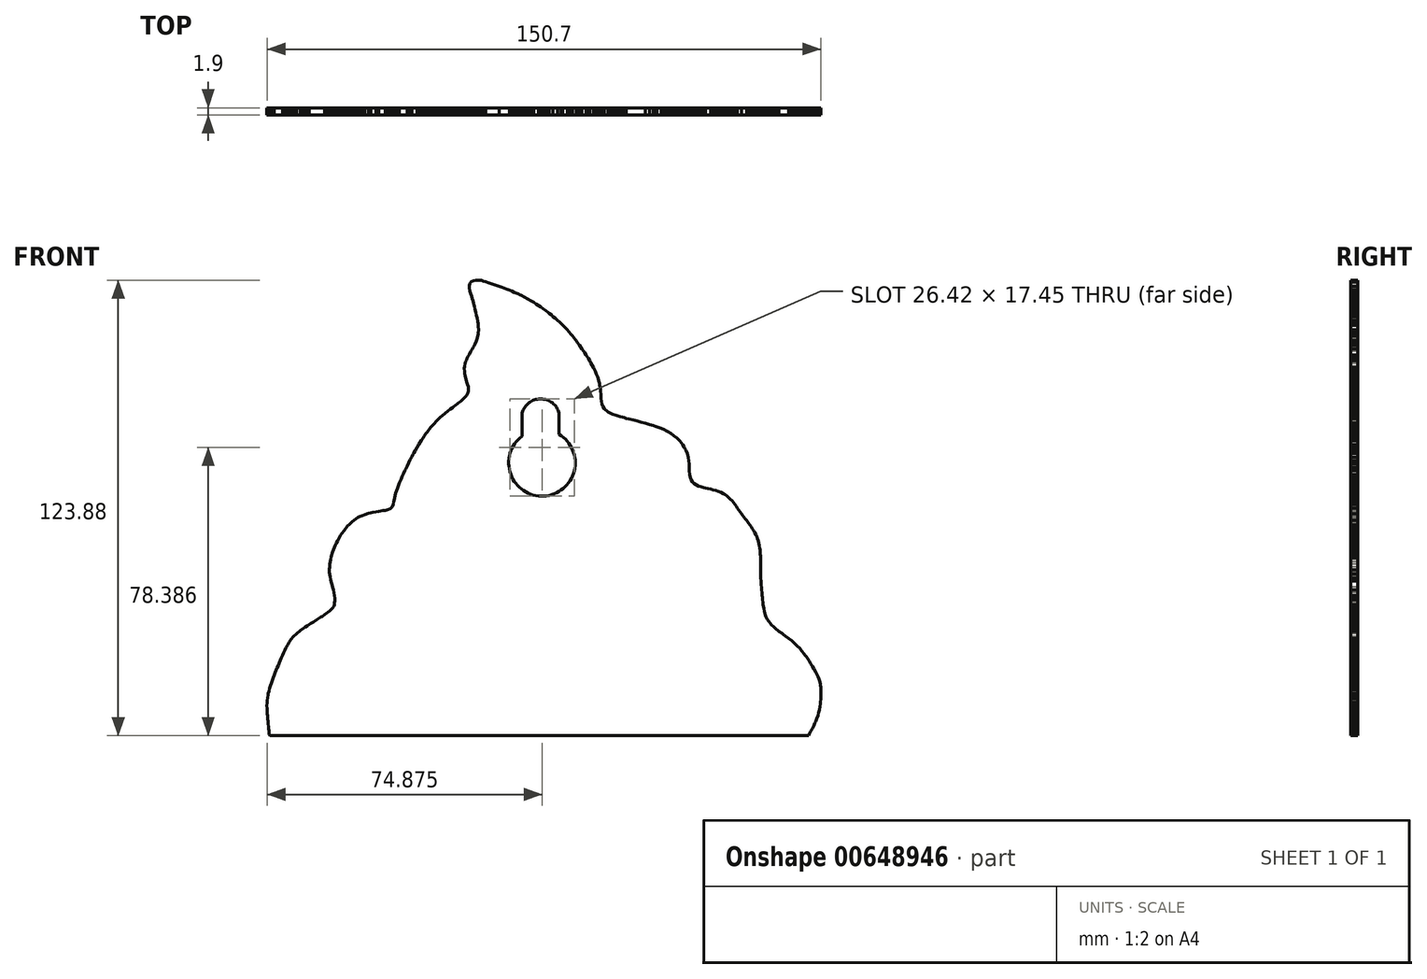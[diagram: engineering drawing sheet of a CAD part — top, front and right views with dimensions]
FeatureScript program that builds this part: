
annotation { "Feature Type Name" : "Feature", "Feature Type Description" : "" }
export const myFeature = defineFeature(function(context is Context, id is Id, definition is map)
    precondition{}
    {
        {
            var Q0;
            Q0=qCreatedBy(makeId("Front.planeOp"),FACE);
            var sketch = newSketch(context, id + "F0", { "sketchPlane" : qUnion([Q0])});
            skLineSegment(sketch, "E0", {"start": v(-3.14, 0.19) * mm, "end": v(-3.1, 0.19) * mm});
            skLineSegment(sketch, "E1", {"start": v(-3.1, 0.19) * mm, "end": v(-3.08, 0.19) * mm});
            skLineSegment(sketch, "E2", {"start": v(-3.08, 0.19) * mm, "end": v(-3.05, 0.19) * mm});
            skLineSegment(sketch, "E3", {"start": v(-3.05, 0.19) * mm, "end": v(-3, 0.19) * mm});
            skLineSegment(sketch, "E4", {"start": v(-3, 0.19) * mm, "end": v(-2.97, 0.19) * mm});
            skLineSegment(sketch, "E5", {"start": v(-2.97, 0.19) * mm, "end": v(-2.94, 0.19) * mm});
            skLineSegment(sketch, "E6", {"start": v(-2.94, 0.19) * mm, "end": v(-2.92, 0.19) * mm});
            skLineSegment(sketch, "E7", {"start": v(-2.92, 0.19) * mm, "end": v(-2.9, 0.19) * mm});
            skLineSegment(sketch, "E8", {"start": v(-2.9, 0.19) * mm, "end": v(-2.86, 0.19) * mm});
            skLineSegment(sketch, "E9", {"start": v(-2.86, 0.19) * mm, "end": v(-2.77, 0.19) * mm});
            skLineSegment(sketch, "E10", {"start": v(-2.77, 0.19) * mm, "end": v(-2.75, 0.19) * mm});
            skLineSegment(sketch, "E11", {"start": v(-2.75, 0.19) * mm, "end": v(-2.72, 0.19) * mm});
            skLineSegment(sketch, "E12", {"start": v(-2.72, 0.19) * mm, "end": v(-2.68, 0.19) * mm});
            skLineSegment(sketch, "E13", {"start": v(-2.68, 0.19) * mm, "end": v(-2.64, 0.19) * mm});
            skLineSegment(sketch, "E14", {"start": v(-2.64, 0.19) * mm, "end": v(-2.53, 0.19) * mm});
            skLineSegment(sketch, "E15", {"start": v(-2.53, 0.19) * mm, "end": v(-2.5, 0.19) * mm});
            skLineSegment(sketch, "E16", {"start": v(-2.5, 0.19) * mm, "end": v(-2.48, 0.19) * mm});
            skLineSegment(sketch, "E17", {"start": v(-2.48, 0.19) * mm, "end": v(-2.46, 0.19) * mm});
            skLineSegment(sketch, "E18", {"start": v(-2.46, 0.19) * mm, "end": v(-2.35, 0.19) * mm});
            skLineSegment(sketch, "E19", {"start": v(-2.35, 0.19) * mm, "end": v(-2.33, 0.19) * mm});
            skLineSegment(sketch, "E20", {"start": v(-2.33, 0.19) * mm, "end": v(-2.3, 0.19) * mm});
            skLineSegment(sketch, "E21", {"start": v(-2.3, 0.19) * mm, "end": v(-2.27, 0.19) * mm});
            skLineSegment(sketch, "E22", {"start": v(-2.27, 0.19) * mm, "end": v(-2.23, 0.19) * mm});
            skLineSegment(sketch, "E23", {"start": v(-2.23, 0.19) * mm, "end": v(-2.2, 0.19) * mm});
            skLineSegment(sketch, "E24", {"start": v(-2.2, 0.19) * mm, "end": v(-2.1, 0.19) * mm});
            skLineSegment(sketch, "E25", {"start": v(-2.1, 0.19) * mm, "end": v(-2.08, 0.19) * mm});
            skLineSegment(sketch, "E26", {"start": v(-2.08, 0.19) * mm, "end": v(-2, 0.19) * mm});
            skLineSegment(sketch, "E27", {"start": v(-2, 0.19) * mm, "end": v(-1.96, 0.19) * mm});
            skLineSegment(sketch, "E28", {"start": v(-1.96, 0.19) * mm, "end": v(-1.94, 0.19) * mm});
            skLineSegment(sketch, "E29", {"start": v(-1.94, 0.19) * mm, "end": v(-1.91, 0.19) * mm});
            skLineSegment(sketch, "E30", {"start": v(-1.91, 0.19) * mm, "end": v(-1.82, 0.19) * mm});
            skLineSegment(sketch, "E31", {"start": v(-1.82, 0.19) * mm, "end": v(-1.8, 0.19) * mm});
            skLineSegment(sketch, "E32", {"start": v(-1.8, 0.19) * mm, "end": v(-1.69, 0.19) * mm});
            skLineSegment(sketch, "E33", {"start": v(-1.69, 0.19) * mm, "end": v(-1.65, 0.19) * mm});
            skLineSegment(sketch, "E34", {"start": v(-1.65, 0.19) * mm, "end": v(-1.62, 0.19) * mm});
            skLineSegment(sketch, "E35", {"start": v(-1.62, 0.19) * mm, "end": v(-1.51, 0.19) * mm});
            skLineSegment(sketch, "E36", {"start": v(-1.51, 0.19) * mm, "end": v(-1.5, 0.19) * mm});
            skLineSegment(sketch, "E37", {"start": v(-1.5, 0.19) * mm, "end": v(-1.45, 0.19) * mm});
            skLineSegment(sketch, "E38", {"start": v(-1.45, 0.19) * mm, "end": v(-1.42, 0.19) * mm});
            skLineSegment(sketch, "E39", {"start": v(-1.42, 0.19) * mm, "end": v(-1.32, 0.19) * mm});
            skLineSegment(sketch, "E40", {"start": v(-1.32, 0.19) * mm, "end": v(-1.3, 0.19) * mm});
            skLineSegment(sketch, "E41", {"start": v(-1.3, 0.19) * mm, "end": v(-1.27, 0.19) * mm});
            skLineSegment(sketch, "E42", {"start": v(-1.27, 0.19) * mm, "end": v(-1.2, 0.19) * mm});
            skLineSegment(sketch, "E43", {"start": v(-1.2, 0.19) * mm, "end": v(-1.18, 0.19) * mm});
            skLineSegment(sketch, "E44", {"start": v(-1.18, 0.19) * mm, "end": v(-1.15, 0.19) * mm});
            skLineSegment(sketch, "E45", {"start": v(-1.15, 0.19) * mm, "end": v(-1.13, 0.19) * mm});
            skLineSegment(sketch, "E46", {"start": v(-1.13, 0.19) * mm, "end": v(-1.1, 0.19) * mm});
            skLineSegment(sketch, "E47", {"start": v(-1.1, 0.19) * mm, "end": v(-1.02, 0.19) * mm});
            skLineSegment(sketch, "E48", {"start": v(-1.02, 0.19) * mm, "end": v(-0.98, 0.19) * mm});
            skLineSegment(sketch, "E49", {"start": v(-0.98, 0.19) * mm, "end": v(-0.95, 0.19) * mm});
            skLineSegment(sketch, "E50", {"start": v(-0.95, 0.19) * mm, "end": v(-0.83, 0.19) * mm});
            skLineSegment(sketch, "E51", {"start": v(-0.83, 0.19) * mm, "end": v(-0.71, 0.19) * mm});
            skLineSegment(sketch, "E52", {"start": v(-0.71, 0.19) * mm, "end": v(-0.69, 0.19) * mm});
            skLineSegment(sketch, "E53", {"start": v(-0.69, 0.19) * mm, "end": v(-0.66, 0.19) * mm});
            skLineSegment(sketch, "E54", {"start": v(-0.66, 0.19) * mm, "end": v(-0.55, 0.19) * mm});
            skLineSegment(sketch, "E55", {"start": v(-0.55, 0.19) * mm, "end": v(-0.44, 0.19) * mm});
            skLineSegment(sketch, "E56", {"start": v(-0.44, 0.19) * mm, "end": v(-0.4, 0.19) * mm});
            skLineSegment(sketch, "E57", {"start": v(-0.4, 0.19) * mm, "end": v(-0.38, 0.19) * mm});
            skLineSegment(sketch, "E58", {"start": v(-0.38, 0.19) * mm, "end": v(-0.29, 0.19) * mm});
            skLineSegment(sketch, "E59", {"start": v(-0.29, 0.19) * mm, "end": v(-0.25, 0.19) * mm});
            skLineSegment(sketch, "E60", {"start": v(-0.25, 0.19) * mm, "end": v(-0.16, 0.19) * mm});
            skLineSegment(sketch, "E61", {"start": v(-0.16, 0.19) * mm, "end": v(-0.14, 0.19) * mm});
            skLineSegment(sketch, "E62", {"start": v(-0.14, 0.19) * mm, "end": v(-0.11, 0.19) * mm});
            skLineSegment(sketch, "E63", {"start": v(-0.11, 0.19) * mm, "end": v(-0.01, 0.19) * mm});
            skLineSegment(sketch, "E64", {"start": v(-0.01, 0.19) * mm, "end": v(0.01, 0.19) * mm});
            skLineSegment(sketch, "E65", {"start": v(0.01, 0.19) * mm, "end": v(0.03, 0.19) * mm});
            skLineSegment(sketch, "E66", {"start": v(0.03, 0.19) * mm, "end": v(0.13, 0.19) * mm});
            skLineSegment(sketch, "E67", {"start": v(0.13, 0.19) * mm, "end": v(0.15, 0.19) * mm});
            skLineSegment(sketch, "E68", {"start": v(0.15, 0.19) * mm, "end": v(0.25, 0.19) * mm});
            skLineSegment(sketch, "E69", {"start": v(0.25, 0.19) * mm, "end": v(0.27, 0.19) * mm});
            skLineSegment(sketch, "E70", {"start": v(0.27, 0.19) * mm, "end": v(0.36, 0.19) * mm});
            skLineSegment(sketch, "E71", {"start": v(0.36, 0.19) * mm, "end": v(0.41, 0.19) * mm});
            skLineSegment(sketch, "E72", {"start": v(0.41, 0.19) * mm, "end": v(0.44, 0.19) * mm});
            skLineSegment(sketch, "E73", {"start": v(0.44, 0.19) * mm, "end": v(0.47, 0.19) * mm});
            skLineSegment(sketch, "E74", {"start": v(0.47, 0.19) * mm, "end": v(0.54, 0.19) * mm});
            skLineSegment(sketch, "E75", {"start": v(0.54, 0.19) * mm, "end": v(0.6, 0.19) * mm});
            skLineSegment(sketch, "E76", {"start": v(0.6, 0.19) * mm, "end": v(0.64, 0.19) * mm});
            skLineSegment(sketch, "E77", {"start": v(0.64, 0.19) * mm, "end": v(0.73, 0.19) * mm});
            skLineSegment(sketch, "E78", {"start": v(0.73, 0.19) * mm, "end": v(0.75, 0.19) * mm});
            skLineSegment(sketch, "E79", {"start": v(0.75, 0.19) * mm, "end": v(0.85, 0.19) * mm});
            skLineSegment(sketch, "E80", {"start": v(0.85, 0.19) * mm, "end": v(0.88, 0.19) * mm});
            skLineSegment(sketch, "E81", {"start": v(0.88, 0.19) * mm, "end": v(0.97, 0.18) * mm});
            skLineSegment(sketch, "E82", {"start": v(0.97, 0.18) * mm, "end": v(1, 0.18) * mm});
            skLineSegment(sketch, "E83", {"start": v(1, 0.18) * mm, "end": v(1.02, 0.18) * mm});
            skLineSegment(sketch, "E84", {"start": v(1.02, 0.18) * mm, "end": v(1.04, 0.18) * mm});
            skLineSegment(sketch, "E85", {"start": v(1.04, 0.18) * mm, "end": v(1.07, 0.18) * mm});
            skLineSegment(sketch, "E86", {"start": v(1.07, 0.18) * mm, "end": v(1.09, 0.18) * mm});
            skLineSegment(sketch, "E87", {"start": v(1.09, 0.18) * mm, "end": v(1.11, 0.18) * mm});
            skLineSegment(sketch, "E88", {"start": v(1.11, 0.18) * mm, "end": v(1.22, 0.18) * mm});
            skLineSegment(sketch, "E89", {"start": v(1.22, 0.18) * mm, "end": v(1.32, 0.18) * mm});
            skLineSegment(sketch, "E90", {"start": v(1.32, 0.18) * mm, "end": v(1.35, 0.18) * mm});
            skLineSegment(sketch, "E91", {"start": v(1.35, 0.18) * mm, "end": v(1.45, 0.18) * mm});
            skLineSegment(sketch, "E92", {"start": v(1.45, 0.18) * mm, "end": v(1.47, 0.18) * mm});
            skLineSegment(sketch, "E93", {"start": v(1.47, 0.18) * mm, "end": v(1.55, 0.18) * mm});
            skLineSegment(sketch, "E94", {"start": v(1.55, 0.18) * mm, "end": v(1.58, 0.18) * mm});
            skLineSegment(sketch, "E95", {"start": v(1.58, 0.18) * mm, "end": v(1.61, 0.18) * mm});
            skLineSegment(sketch, "E96", {"start": v(1.61, 0.18) * mm, "end": v(1.64, 0.18) * mm});
            skLineSegment(sketch, "E97", {"start": v(1.64, 0.18) * mm, "end": v(1.7, 0.18) * mm});
            skLineSegment(sketch, "E98", {"start": v(1.7, 0.18) * mm, "end": v(1.73, 0.18) * mm});
            skLineSegment(sketch, "E99", {"start": v(1.73, 0.18) * mm, "end": v(1.76, 0.18) * mm});
            skLineSegment(sketch, "E100", {"start": v(1.76, 0.18) * mm, "end": v(1.81, 0.18) * mm});
            skLineSegment(sketch, "E101", {"start": v(1.81, 0.18) * mm, "end": v(1.9, 0.18) * mm});
            skLineSegment(sketch, "E102", {"start": v(1.9, 0.18) * mm, "end": v(1.91, 0.18) * mm});
            skLineSegment(sketch, "E103", {"start": v(1.91, 0.18) * mm, "end": v(1.94, 0.18) * mm});
            skLineSegment(sketch, "E104", {"start": v(1.94, 0.18) * mm, "end": v(1.97, 0.18) * mm});
            skLineSegment(sketch, "E105", {"start": v(1.97, 0.18) * mm, "end": v(2.03, 0.18) * mm});
            skLineSegment(sketch, "E106", {"start": v(2.03, 0.18) * mm, "end": v(2.06, 0.18) * mm});
            skLineSegment(sketch, "E107", {"start": v(2.06, 0.18) * mm, "end": v(2.09, 0.18) * mm});
            skLineSegment(sketch, "E108", {"start": v(2.09, 0.18) * mm, "end": v(2.12, 0.18) * mm});
            skLineSegment(sketch, "E109", {"start": v(2.12, 0.18) * mm, "end": v(2.16, 0.18) * mm});
            skLineSegment(sketch, "E110", {"start": v(2.16, 0.18) * mm, "end": v(2.2, 0.18) * mm});
            skLineSegment(sketch, "E111", {"start": v(2.2, 0.18) * mm, "end": v(2.22, 0.18) * mm});
            skLineSegment(sketch, "E112", {"start": v(2.22, 0.18) * mm, "end": v(2.3, 0.18) * mm});
            skLineSegment(sketch, "E113", {"start": v(2.3, 0.18) * mm, "end": v(2.34, 0.18) * mm});
            skLineSegment(sketch, "E114", {"start": v(2.34, 0.18) * mm, "end": v(2.36, 0.18) * mm});
            skLineSegment(sketch, "E115", {"start": v(2.36, 0.18) * mm, "end": v(2.38, 0.18) * mm});
            skLineSegment(sketch, "E116", {"start": v(2.38, 0.18) * mm, "end": v(2.45, 0.18) * mm});
            skLineSegment(sketch, "E117", {"start": v(2.45, 0.18) * mm, "end": v(2.47, 0.18) * mm});
            skLineSegment(sketch, "E118", {"start": v(2.47, 0.18) * mm, "end": v(2.5, 0.18) * mm});
            skLineSegment(sketch, "E119", {"start": v(2.5, 0.18) * mm, "end": v(2.52, 0.18) * mm});
            skLineSegment(sketch, "E120", {"start": v(2.52, 0.18) * mm, "end": v(2.56, 0.18) * mm});
            skLineSegment(sketch, "E121", {"start": v(2.56, 0.18) * mm, "end": v(2.66, 0.18) * mm});
            skLineSegment(sketch, "E122", {"start": v(2.66, 0.18) * mm, "end": v(2.69, 0.18) * mm});
            skLineSegment(sketch, "E123", {"start": v(2.69, 0.18) * mm, "end": v(2.8, 0.18) * mm});
            skLineSegment(sketch, "E124", {"start": v(2.8, 0.18) * mm, "end": v(2.83, 0.18) * mm});
            skLineSegment(sketch, "E125", {"start": v(2.83, 0.18) * mm, "end": v(2.86, 0.18) * mm});
            skLineSegment(sketch, "E126", {"start": v(2.86, 0.18) * mm, "end": v(2.9, 0.18) * mm});
            skLineSegment(sketch, "E127", {"start": v(2.9, 0.18) * mm, "end": v(2.92, 0.18) * mm});
            skLineSegment(sketch, "E128", {"start": v(2.92, 0.18) * mm, "end": v(2.95, 0.18) * mm});
            skLineSegment(sketch, "E129", {"start": v(2.95, 0.18) * mm, "end": v(3.06, 0.18) * mm});
            skLineSegment(sketch, "E130", {"start": v(3.06, 0.18) * mm, "end": v(3.09, 0.18) * mm});
            skLineSegment(sketch, "E131", {"start": v(3.09, 0.18) * mm, "end": v(3.1, 0.18) * mm});
            skLineSegment(sketch, "E132", {"start": v(3.1, 0.18) * mm, "end": v(3.13, 0.18) * mm});
            skLineSegment(sketch, "E133", {"start": v(3.13, 0.18) * mm, "end": v(3.24, 0.18) * mm});
            skLineSegment(sketch, "E134", {"start": v(3.24, 0.18) * mm, "end": v(3.26, 0.18) * mm});
            skLineSegment(sketch, "E135", {"start": v(3.26, 0.18) * mm, "end": v(3.29, 0.18) * mm});
            skLineSegment(sketch, "E136", {"start": v(3.29, 0.18) * mm, "end": v(3.3, 0.18) * mm});
            skLineSegment(sketch, "E137", {"start": v(3.3, 0.18) * mm, "end": v(3.33, 0.18) * mm});
            skLineSegment(sketch, "E138", {"start": v(3.33, 0.18) * mm, "end": v(3.35, 0.18) * mm});
            skLineSegment(sketch, "E139", {"start": v(3.35, 0.18) * mm, "end": v(3.37, 0.18) * mm});
            skLineSegment(sketch, "E140", {"start": v(3.37, 0.18) * mm, "end": v(3.4, 0.18) * mm});
            skLineSegment(sketch, "E141", {"start": v(3.4, 0.18) * mm, "end": v(3.42, 0.18) * mm});
            skLineSegment(sketch, "E142", {"start": v(3.42, 0.18) * mm, "end": v(3.52, 0.18) * mm});
            skLineSegment(sketch, "E143", {"start": v(3.52, 0.18) * mm, "end": v(3.56, 0.18) * mm});
            skLineSegment(sketch, "E144", {"start": v(3.56, 0.18) * mm, "end": v(3.59, 0.18) * mm});
            skLineSegment(sketch, "E145", {"start": v(3.59, 0.18) * mm, "end": v(3.62, 0.18) * mm});
            skLineSegment(sketch, "E146", {"start": v(3.62, 0.18) * mm, "end": v(3.64, 0.18) * mm});
            skLineSegment(sketch, "E147", {"start": v(3.64, 0.18) * mm, "end": v(3.67, 0.18) * mm});
            skLineSegment(sketch, "E148", {"start": v(3.67, 0.18) * mm, "end": v(3.82, 0.18) * mm});
            skLineSegment(sketch, "E149", {"start": v(3.82, 0.18) * mm, "end": v(3.84, 0.18) * mm});
            skLineSegment(sketch, "E150", {"start": v(3.84, 0.18) * mm, "end": v(4, 0.18) * mm});
            skLineSegment(sketch, "E151", {"start": v(4, 0.18) * mm, "end": v(4.03, 0.18) * mm});
            skLineSegment(sketch, "E152", {"start": v(4.03, 0.18) * mm, "end": v(4.06, 0.18) * mm});
            skLineSegment(sketch, "E153", {"start": v(4.06, 0.18) * mm, "end": v(4.08, 0.18) * mm});
            skLineSegment(sketch, "E154", {"start": v(4.08, 0.18) * mm, "end": v(4.1, 0.18) * mm});
            skLineSegment(sketch, "E155", {"start": v(4.1, 0.18) * mm, "end": v(4.14, 0.18) * mm});
            skLineSegment(sketch, "E156", {"start": v(4.14, 0.18) * mm, "end": v(4.26, 0.18) * mm});
            skLineSegment(sketch, "E157", {"start": v(4.26, 0.18) * mm, "end": v(4.37, 0.18) * mm});
            skLineSegment(sketch, "E158", {"start": v(4.37, 0.18) * mm, "end": v(4.41, 0.18) * mm});
            skLineSegment(sketch, "E159", {"start": v(4.41, 0.18) * mm, "end": v(4.47, 0.18) * mm});
            skLineSegment(sketch, "E160", {"start": v(4.47, 0.18) * mm, "end": v(4.49, 0.18) * mm});
            skLineSegment(sketch, "E161", {"start": v(4.49, 0.18) * mm, "end": v(4.5, 0.18) * mm});
            skLineSegment(sketch, "E162", {"start": v(4.5, 0.18) * mm, "end": v(4.55, 0.18) * mm});
            skLineSegment(sketch, "E163", {"start": v(4.55, 0.18) * mm, "end": v(4.57, 0.18) * mm});
            skLineSegment(sketch, "E164", {"start": v(4.57, 0.18) * mm, "end": v(4.58, 0.2) * mm});
            skLineSegment(sketch, "E165", {"start": v(4.58, 0.2) * mm, "end": v(4.6, 0.25) * mm});
            skLineSegment(sketch, "E166", {"start": v(4.6, 0.25) * mm, "end": v(4.61, 0.27) * mm});
            skLineSegment(sketch, "E167", {"start": v(4.61, 0.27) * mm, "end": v(4.62, 0.29) * mm});
            skLineSegment(sketch, "E168", {"start": v(4.62, 0.29) * mm, "end": v(4.64, 0.33) * mm});
            skLineSegment(sketch, "E169", {"start": v(4.64, 0.33) * mm, "end": v(4.66, 0.36) * mm});
            skLineSegment(sketch, "E170", {"start": v(4.66, 0.36) * mm, "end": v(4.67, 0.38) * mm});
            skLineSegment(sketch, "E171", {"start": v(4.67, 0.38) * mm, "end": v(4.68, 0.4) * mm});
            skLineSegment(sketch, "E172", {"start": v(4.68, 0.4) * mm, "end": v(4.69, 0.43) * mm});
            skLineSegment(sketch, "E173", {"start": v(4.69, 0.43) * mm, "end": v(4.7, 0.47) * mm});
            skLineSegment(sketch, "E174", {"start": v(4.7, 0.47) * mm, "end": v(4.72, 0.52) * mm});
            skLineSegment(sketch, "E175", {"start": v(4.72, 0.52) * mm, "end": v(4.73, 0.55) * mm});
            skLineSegment(sketch, "E176", {"start": v(4.73, 0.55) * mm, "end": v(4.73, 0.6) * mm});
            skLineSegment(sketch, "E177", {"start": v(4.73, 0.6) * mm, "end": v(4.74, 0.64) * mm});
            skLineSegment(sketch, "E178", {"start": v(4.74, 0.64) * mm, "end": v(4.74, 0.66) * mm});
            skLineSegment(sketch, "E179", {"start": v(4.74, 0.66) * mm, "end": v(4.75, 0.71) * mm});
            skLineSegment(sketch, "E180", {"start": v(4.75, 0.71) * mm, "end": v(4.75, 0.76) * mm});
            skLineSegment(sketch, "E181", {"start": v(4.75, 0.76) * mm, "end": v(4.75, 0.79) * mm});
            skLineSegment(sketch, "E182", {"start": v(4.75, 0.79) * mm, "end": v(4.75, 0.84) * mm});
            skLineSegment(sketch, "E183", {"start": v(4.75, 0.84) * mm, "end": v(4.74, 0.88) * mm});
            skLineSegment(sketch, "E184", {"start": v(4.74, 0.88) * mm, "end": v(4.74, 0.9) * mm});
            skLineSegment(sketch, "E185", {"start": v(4.74, 0.9) * mm, "end": v(4.74, 0.92) * mm});
            skLineSegment(sketch, "E186", {"start": v(4.74, 0.92) * mm, "end": v(4.73, 0.95) * mm});
            skLineSegment(sketch, "E187", {"start": v(4.73, 0.95) * mm, "end": v(4.72, 1) * mm});
            skLineSegment(sketch, "E188", {"start": v(4.72, 1) * mm, "end": v(4.7, 1.03) * mm});
            skLineSegment(sketch, "E189", {"start": v(4.7, 1.03) * mm, "end": v(4.69, 1.07) * mm});
            skLineSegment(sketch, "E190", {"start": v(4.69, 1.07) * mm, "end": v(4.67, 1.1) * mm});
            skLineSegment(sketch, "E191", {"start": v(4.67, 1.1) * mm, "end": v(4.65, 1.14) * mm});
            skLineSegment(sketch, "E192", {"start": v(4.65, 1.14) * mm, "end": v(4.63, 1.18) * mm});
            skLineSegment(sketch, "E193", {"start": v(4.63, 1.18) * mm, "end": v(4.6, 1.22) * mm});
            skLineSegment(sketch, "E194", {"start": v(4.6, 1.22) * mm, "end": v(4.58, 1.26) * mm});
            skLineSegment(sketch, "E195", {"start": v(4.58, 1.26) * mm, "end": v(4.55, 1.3) * mm});
            skLineSegment(sketch, "E196", {"start": v(4.55, 1.3) * mm, "end": v(4.54, 1.31) * mm});
            skLineSegment(sketch, "E197", {"start": v(4.54, 1.31) * mm, "end": v(4.52, 1.33) * mm});
            skLineSegment(sketch, "E198", {"start": v(4.52, 1.33) * mm, "end": v(4.5, 1.36) * mm});
            skLineSegment(sketch, "E199", {"start": v(4.5, 1.36) * mm, "end": v(4.48, 1.4) * mm});
            skLineSegment(sketch, "E200", {"start": v(4.48, 1.4) * mm, "end": v(4.44, 1.43) * mm});
            skLineSegment(sketch, "E201", {"start": v(4.44, 1.43) * mm, "end": v(4.4, 1.47) * mm});
            skLineSegment(sketch, "E202", {"start": v(4.4, 1.47) * mm, "end": v(4.39, 1.5) * mm});
            skLineSegment(sketch, "E203", {"start": v(4.39, 1.5) * mm, "end": v(4.36, 1.52) * mm});
            skLineSegment(sketch, "E204", {"start": v(4.36, 1.52) * mm, "end": v(4.33, 1.54) * mm});
            skLineSegment(sketch, "E205", {"start": v(4.33, 1.54) * mm, "end": v(4.29, 1.58) * mm});
            skLineSegment(sketch, "E206", {"start": v(4.29, 1.58) * mm, "end": v(4.24, 1.61) * mm});
            skLineSegment(sketch, "E207", {"start": v(4.24, 1.61) * mm, "end": v(4.2, 1.63) * mm});
            skLineSegment(sketch, "E208", {"start": v(4.2, 1.63) * mm, "end": v(4.2, 1.65) * mm});
            skLineSegment(sketch, "E209", {"start": v(4.2, 1.65) * mm, "end": v(4.15, 1.68) * mm});
            skLineSegment(sketch, "E210", {"start": v(4.15, 1.68) * mm, "end": v(4.13, 1.7) * mm});
            skLineSegment(sketch, "E211", {"start": v(4.13, 1.7) * mm, "end": v(4.1, 1.71) * mm});
            skLineSegment(sketch, "E212", {"start": v(4.1, 1.71) * mm, "end": v(4.07, 1.74) * mm});
            skLineSegment(sketch, "E213", {"start": v(4.07, 1.74) * mm, "end": v(4.04, 1.77) * mm});
            skLineSegment(sketch, "E214", {"start": v(4.04, 1.77) * mm, "end": v(4.02, 1.8) * mm});
            skLineSegment(sketch, "E215", {"start": v(4.02, 1.8) * mm, "end": v(4, 1.81) * mm});
            skLineSegment(sketch, "E216", {"start": v(4, 1.81) * mm, "end": v(3.98, 1.85) * mm});
            skLineSegment(sketch, "E217", {"start": v(3.98, 1.85) * mm, "end": v(3.96, 1.9) * mm});
            skLineSegment(sketch, "E218", {"start": v(3.96, 1.9) * mm, "end": v(3.95, 1.91) * mm});
            skLineSegment(sketch, "E219", {"start": v(3.95, 1.91) * mm, "end": v(3.94, 1.94) * mm});
            skLineSegment(sketch, "E220", {"start": v(3.94, 1.94) * mm, "end": v(3.94, 1.96) * mm});
            skLineSegment(sketch, "E221", {"start": v(3.94, 1.96) * mm, "end": v(3.93, 2) * mm});
            skLineSegment(sketch, "E222", {"start": v(3.93, 2) * mm, "end": v(3.92, 2.03) * mm});
            skLineSegment(sketch, "E223", {"start": v(3.92, 2.03) * mm, "end": v(3.92, 2.06) * mm});
            skLineSegment(sketch, "E224", {"start": v(3.92, 2.06) * mm, "end": v(3.92, 2.1) * mm});
            skLineSegment(sketch, "E225", {"start": v(3.92, 2.1) * mm, "end": v(3.91, 2.13) * mm});
            skLineSegment(sketch, "E226", {"start": v(3.91, 2.13) * mm, "end": v(3.9, 2.17) * mm});
            skLineSegment(sketch, "E227", {"start": v(3.9, 2.17) * mm, "end": v(3.9, 2.19) * mm});
            skLineSegment(sketch, "E228", {"start": v(3.9, 2.19) * mm, "end": v(3.9, 2.23) * mm});
            skLineSegment(sketch, "E229", {"start": v(3.9, 2.23) * mm, "end": v(3.9, 2.27) * mm});
            skLineSegment(sketch, "E230", {"start": v(3.9, 2.27) * mm, "end": v(3.9, 2.3) * mm});
            skLineSegment(sketch, "E231", {"start": v(3.9, 2.3) * mm, "end": v(3.9, 2.35) * mm});
            skLineSegment(sketch, "E232", {"start": v(3.9, 2.35) * mm, "end": v(3.9, 2.4) * mm});
            skLineSegment(sketch, "E233", {"start": v(3.9, 2.4) * mm, "end": v(3.89, 2.44) * mm});
            skLineSegment(sketch, "E234", {"start": v(3.89, 2.44) * mm, "end": v(3.89, 2.47) * mm});
            skLineSegment(sketch, "E235", {"start": v(3.89, 2.47) * mm, "end": v(3.89, 2.5) * mm});
            skLineSegment(sketch, "E236", {"start": v(3.89, 2.5) * mm, "end": v(3.89, 2.53) * mm});
            skLineSegment(sketch, "E237", {"start": v(3.89, 2.53) * mm, "end": v(3.88, 2.56) * mm});
            skLineSegment(sketch, "E238", {"start": v(3.88, 2.56) * mm, "end": v(3.88, 2.58) * mm});
            skLineSegment(sketch, "E239", {"start": v(3.88, 2.58) * mm, "end": v(3.88, 2.63) * mm});
            skLineSegment(sketch, "E240", {"start": v(3.88, 2.63) * mm, "end": v(3.88, 2.67) * mm});
            skLineSegment(sketch, "E241", {"start": v(3.88, 2.67) * mm, "end": v(3.88, 2.7) * mm});
            skLineSegment(sketch, "E242", {"start": v(3.88, 2.7) * mm, "end": v(3.88, 2.73) * mm});
            skLineSegment(sketch, "E243", {"start": v(3.88, 2.73) * mm, "end": v(3.88, 2.76) * mm});
            skLineSegment(sketch, "E244", {"start": v(3.88, 2.76) * mm, "end": v(3.88, 2.78) * mm});
            skLineSegment(sketch, "E245", {"start": v(3.88, 2.78) * mm, "end": v(3.88, 2.81) * mm});
            skLineSegment(sketch, "E246", {"start": v(3.88, 2.81) * mm, "end": v(3.88, 2.84) * mm});
            skLineSegment(sketch, "E247", {"start": v(3.88, 2.84) * mm, "end": v(3.87, 2.87) * mm});
            skLineSegment(sketch, "E248", {"start": v(3.87, 2.87) * mm, "end": v(3.87, 2.9) * mm});
            skLineSegment(sketch, "E249", {"start": v(3.87, 2.9) * mm, "end": v(3.86, 2.94) * mm});
            skLineSegment(sketch, "E250", {"start": v(3.86, 2.94) * mm, "end": v(3.85, 2.97) * mm});
            skLineSegment(sketch, "E251", {"start": v(3.85, 2.97) * mm, "end": v(3.84, 3) * mm});
            skLineSegment(sketch, "E252", {"start": v(3.84, 3) * mm, "end": v(3.83, 3.03) * mm});
            skLineSegment(sketch, "E253", {"start": v(3.83, 3.03) * mm, "end": v(3.81, 3.06) * mm});
            skLineSegment(sketch, "E254", {"start": v(3.81, 3.06) * mm, "end": v(3.8, 3.1) * mm});
            skLineSegment(sketch, "E255", {"start": v(3.8, 3.1) * mm, "end": v(3.78, 3.12) * mm});
            skLineSegment(sketch, "E256", {"start": v(3.78, 3.12) * mm, "end": v(3.77, 3.15) * mm});
            skLineSegment(sketch, "E257", {"start": v(3.77, 3.15) * mm, "end": v(3.75, 3.17) * mm});
            skLineSegment(sketch, "E258", {"start": v(3.75, 3.17) * mm, "end": v(3.73, 3.2) * mm});
            skLineSegment(sketch, "E259", {"start": v(3.73, 3.2) * mm, "end": v(3.71, 3.23) * mm});
            skLineSegment(sketch, "E260", {"start": v(3.71, 3.23) * mm, "end": v(3.7, 3.25) * mm});
            skLineSegment(sketch, "E261", {"start": v(3.7, 3.25) * mm, "end": v(3.68, 3.26) * mm});
            skLineSegment(sketch, "E262", {"start": v(3.68, 3.26) * mm, "end": v(3.66, 3.29) * mm});
            skLineSegment(sketch, "E263", {"start": v(3.66, 3.29) * mm, "end": v(3.65, 3.31) * mm});
            skLineSegment(sketch, "E264", {"start": v(3.65, 3.31) * mm, "end": v(3.63, 3.34) * mm});
            skLineSegment(sketch, "E265", {"start": v(3.63, 3.34) * mm, "end": v(3.61, 3.36) * mm});
            skLineSegment(sketch, "E266", {"start": v(3.61, 3.36) * mm, "end": v(3.6, 3.39) * mm});
            skLineSegment(sketch, "E267", {"start": v(3.6, 3.39) * mm, "end": v(3.57, 3.41) * mm});
            skLineSegment(sketch, "E268", {"start": v(3.57, 3.41) * mm, "end": v(3.55, 3.44) * mm});
            skLineSegment(sketch, "E269", {"start": v(3.55, 3.44) * mm, "end": v(3.53, 3.47) * mm});
            skLineSegment(sketch, "E270", {"start": v(3.53, 3.47) * mm, "end": v(3.51, 3.5) * mm});
            skLineSegment(sketch, "E271", {"start": v(3.51, 3.5) * mm, "end": v(3.5, 3.52) * mm});
            skLineSegment(sketch, "E272", {"start": v(3.5, 3.52) * mm, "end": v(3.47, 3.54) * mm});
            skLineSegment(sketch, "E273", {"start": v(3.47, 3.54) * mm, "end": v(3.45, 3.57) * mm});
            skLineSegment(sketch, "E274", {"start": v(3.45, 3.57) * mm, "end": v(3.43, 3.6) * mm});
            skLineSegment(sketch, "E275", {"start": v(3.43, 3.6) * mm, "end": v(3.4, 3.61) * mm});
            skLineSegment(sketch, "E276", {"start": v(3.4, 3.61) * mm, "end": v(3.38, 3.63) * mm});
            skLineSegment(sketch, "E277", {"start": v(3.38, 3.63) * mm, "end": v(3.35, 3.65) * mm});
            skLineSegment(sketch, "E278", {"start": v(3.35, 3.65) * mm, "end": v(3.31, 3.67) * mm});
            skLineSegment(sketch, "E279", {"start": v(3.31, 3.67) * mm, "end": v(3.28, 3.68) * mm});
            skLineSegment(sketch, "E280", {"start": v(3.28, 3.68) * mm, "end": v(3.24, 3.7) * mm});
            skLineSegment(sketch, "E281", {"start": v(3.24, 3.7) * mm, "end": v(3.2, 3.7) * mm});
            skLineSegment(sketch, "E282", {"start": v(3.2, 3.7) * mm, "end": v(3.17, 3.71) * mm});
            skLineSegment(sketch, "E283", {"start": v(3.17, 3.71) * mm, "end": v(3.13, 3.72) * mm});
            skLineSegment(sketch, "E284", {"start": v(3.13, 3.72) * mm, "end": v(3.1, 3.73) * mm});
            skLineSegment(sketch, "E285", {"start": v(3.1, 3.73) * mm, "end": v(3.07, 3.74) * mm});
            skLineSegment(sketch, "E286", {"start": v(3.07, 3.74) * mm, "end": v(3.03, 3.75) * mm});
            skLineSegment(sketch, "E287", {"start": v(3.03, 3.75) * mm, "end": v(3, 3.76) * mm});
            skLineSegment(sketch, "E288", {"start": v(3, 3.76) * mm, "end": v(2.96, 3.77) * mm});
            skLineSegment(sketch, "E289", {"start": v(2.96, 3.77) * mm, "end": v(2.93, 3.8) * mm});
            skLineSegment(sketch, "E290", {"start": v(2.93, 3.8) * mm, "end": v(2.9, 3.82) * mm});
            skLineSegment(sketch, "E291", {"start": v(2.9, 3.82) * mm, "end": v(2.89, 3.85) * mm});
            skLineSegment(sketch, "E292", {"start": v(2.89, 3.85) * mm, "end": v(2.87, 3.89) * mm});
            skLineSegment(sketch, "E293", {"start": v(2.87, 3.89) * mm, "end": v(2.87, 3.92) * mm});
            skLineSegment(sketch, "E294", {"start": v(2.87, 3.92) * mm, "end": v(2.87, 3.97) * mm});
            skLineSegment(sketch, "E295", {"start": v(2.87, 3.97) * mm, "end": v(2.86, 4.02) * mm});
            skLineSegment(sketch, "E296", {"start": v(2.86, 4.02) * mm, "end": v(2.86, 4.08) * mm});
            skLineSegment(sketch, "E297", {"start": v(2.86, 4.08) * mm, "end": v(2.86, 4.11) * mm});
            skLineSegment(sketch, "E298", {"start": v(2.86, 4.11) * mm, "end": v(2.85, 4.17) * mm});
            skLineSegment(sketch, "E299", {"start": v(2.85, 4.17) * mm, "end": v(2.83, 4.22) * mm});
            skLineSegment(sketch, "E300", {"start": v(2.83, 4.22) * mm, "end": v(2.81, 4.27) * mm});
            skLineSegment(sketch, "E301", {"start": v(2.81, 4.27) * mm, "end": v(2.8, 4.3) * mm});
            skLineSegment(sketch, "E302", {"start": v(2.8, 4.3) * mm, "end": v(2.8, 4.32) * mm});
            skLineSegment(sketch, "E303", {"start": v(2.8, 4.32) * mm, "end": v(2.77, 4.35) * mm});
            skLineSegment(sketch, "E304", {"start": v(2.77, 4.35) * mm, "end": v(2.73, 4.4) * mm});
            skLineSegment(sketch, "E305", {"start": v(2.73, 4.4) * mm, "end": v(2.69, 4.44) * mm});
            skLineSegment(sketch, "E306", {"start": v(2.69, 4.44) * mm, "end": v(2.64, 4.48) * mm});
            skLineSegment(sketch, "E307", {"start": v(2.64, 4.48) * mm, "end": v(2.6, 4.5) * mm});
            skLineSegment(sketch, "E308", {"start": v(2.6, 4.5) * mm, "end": v(2.55, 4.54) * mm});
            skLineSegment(sketch, "E309", {"start": v(2.55, 4.54) * mm, "end": v(2.53, 4.55) * mm});
            skLineSegment(sketch, "E310", {"start": v(2.53, 4.55) * mm, "end": v(2.5, 4.56) * mm});
            skLineSegment(sketch, "E311", {"start": v(2.5, 4.56) * mm, "end": v(2.46, 4.58) * mm});
            skLineSegment(sketch, "E312", {"start": v(2.46, 4.58) * mm, "end": v(2.4, 4.6) * mm});
            skLineSegment(sketch, "E313", {"start": v(2.4, 4.6) * mm, "end": v(2.38, 4.61) * mm});
            skLineSegment(sketch, "E314", {"start": v(2.38, 4.61) * mm, "end": v(2.35, 4.62) * mm});
            skLineSegment(sketch, "E315", {"start": v(2.35, 4.62) * mm, "end": v(2.3, 4.64) * mm});
            skLineSegment(sketch, "E316", {"start": v(2.3, 4.64) * mm, "end": v(2.23, 4.66) * mm});
            skLineSegment(sketch, "E317", {"start": v(2.23, 4.66) * mm, "end": v(2.17, 4.67) * mm});
            skLineSegment(sketch, "E318", {"start": v(2.17, 4.67) * mm, "end": v(2.11, 4.69) * mm});
            skLineSegment(sketch, "E319", {"start": v(2.11, 4.69) * mm, "end": v(2.06, 4.7) * mm});
            skLineSegment(sketch, "E320", {"start": v(2.06, 4.7) * mm, "end": v(2, 4.72) * mm});
            skLineSegment(sketch, "E321", {"start": v(2, 4.72) * mm, "end": v(1.96, 4.73) * mm});
            skLineSegment(sketch, "E322", {"start": v(1.96, 4.73) * mm, "end": v(1.93, 4.73) * mm});
            skLineSegment(sketch, "E323", {"start": v(1.93, 4.73) * mm, "end": v(1.9, 4.74) * mm});
            skLineSegment(sketch, "E324", {"start": v(1.9, 4.74) * mm, "end": v(1.88, 4.75) * mm});
            skLineSegment(sketch, "E325", {"start": v(1.88, 4.75) * mm, "end": v(1.85, 4.76) * mm});
            skLineSegment(sketch, "E326", {"start": v(1.85, 4.76) * mm, "end": v(1.81, 4.77) * mm});
            skLineSegment(sketch, "E327", {"start": v(1.81, 4.77) * mm, "end": v(1.77, 4.79) * mm});
            skLineSegment(sketch, "E328", {"start": v(1.77, 4.79) * mm, "end": v(1.72, 4.8) * mm});
            skLineSegment(sketch, "E329", {"start": v(1.72, 4.8) * mm, "end": v(1.7, 4.82) * mm});
            skLineSegment(sketch, "E330", {"start": v(1.7, 4.82) * mm, "end": v(1.64, 4.86) * mm});
            skLineSegment(sketch, "E331", {"start": v(1.64, 4.86) * mm, "end": v(1.62, 4.9) * mm});
            skLineSegment(sketch, "E332", {"start": v(1.62, 4.9) * mm, "end": v(1.6, 4.93) * mm});
            skLineSegment(sketch, "E333", {"start": v(1.6, 4.93) * mm, "end": v(1.6, 4.97) * mm});
            skLineSegment(sketch, "E334", {"start": v(1.6, 4.97) * mm, "end": v(1.6, 5.01) * mm});
            skLineSegment(sketch, "E335", {"start": v(1.6, 5.01) * mm, "end": v(1.6, 5.04) * mm});
            skLineSegment(sketch, "E336", {"start": v(1.6, 5.04) * mm, "end": v(1.6, 5.07) * mm});
            skLineSegment(sketch, "E337", {"start": v(1.6, 5.07) * mm, "end": v(1.6, 5.11) * mm});
            skLineSegment(sketch, "E338", {"start": v(1.6, 5.11) * mm, "end": v(1.59, 5.15) * mm});
            skLineSegment(sketch, "E339", {"start": v(1.59, 5.15) * mm, "end": v(1.59, 5.17) * mm});
            skLineSegment(sketch, "E340", {"start": v(1.59, 5.17) * mm, "end": v(1.58, 5.2) * mm});
            skLineSegment(sketch, "E341", {"start": v(1.58, 5.2) * mm, "end": v(1.58, 5.23) * mm});
            skLineSegment(sketch, "E342", {"start": v(1.58, 5.23) * mm, "end": v(1.57, 5.26) * mm});
            skLineSegment(sketch, "E343", {"start": v(1.57, 5.26) * mm, "end": v(1.56, 5.3) * mm});
            skLineSegment(sketch, "E344", {"start": v(1.56, 5.3) * mm, "end": v(1.55, 5.32) * mm});
            skLineSegment(sketch, "E345", {"start": v(1.55, 5.32) * mm, "end": v(1.53, 5.36) * mm});
            skLineSegment(sketch, "E346", {"start": v(1.53, 5.36) * mm, "end": v(1.52, 5.4) * mm});
            skLineSegment(sketch, "E347", {"start": v(1.52, 5.4) * mm, "end": v(1.5, 5.43) * mm});
            skLineSegment(sketch, "E348", {"start": v(1.5, 5.43) * mm, "end": v(1.5, 5.45) * mm});
            skLineSegment(sketch, "E349", {"start": v(1.5, 5.45) * mm, "end": v(1.47, 5.49) * mm});
            skLineSegment(sketch, "E350", {"start": v(1.47, 5.49) * mm, "end": v(1.45, 5.52) * mm});
            skLineSegment(sketch, "E351", {"start": v(1.45, 5.52) * mm, "end": v(1.44, 5.55) * mm});
            skLineSegment(sketch, "E352", {"start": v(1.44, 5.55) * mm, "end": v(1.42, 5.59) * mm});
            skLineSegment(sketch, "E353", {"start": v(1.42, 5.59) * mm, "end": v(1.4, 5.61) * mm});
            skLineSegment(sketch, "E354", {"start": v(1.4, 5.61) * mm, "end": v(1.39, 5.64) * mm});
            skLineSegment(sketch, "E355", {"start": v(1.39, 5.64) * mm, "end": v(1.36, 5.67) * mm});
            skLineSegment(sketch, "E356", {"start": v(1.36, 5.67) * mm, "end": v(1.35, 5.69) * mm});
            skLineSegment(sketch, "E357", {"start": v(1.35, 5.69) * mm, "end": v(1.33, 5.72) * mm});
            skLineSegment(sketch, "E358", {"start": v(1.33, 5.72) * mm, "end": v(1.29, 5.78) * mm});
            skLineSegment(sketch, "E359", {"start": v(1.29, 5.78) * mm, "end": v(1.26, 5.81) * mm});
            skLineSegment(sketch, "E360", {"start": v(1.26, 5.81) * mm, "end": v(1.24, 5.84) * mm});
            skLineSegment(sketch, "E361", {"start": v(1.24, 5.84) * mm, "end": v(1.23, 5.86) * mm});
            skLineSegment(sketch, "E362", {"start": v(1.23, 5.86) * mm, "end": v(1.21, 5.88) * mm});
            skLineSegment(sketch, "E363", {"start": v(1.21, 5.88) * mm, "end": v(1.2, 5.9) * mm});
            skLineSegment(sketch, "E364", {"start": v(1.2, 5.9) * mm, "end": v(1.17, 5.93) * mm});
            skLineSegment(sketch, "E365", {"start": v(1.17, 5.93) * mm, "end": v(1.14, 5.97) * mm});
            skLineSegment(sketch, "E366", {"start": v(1.14, 5.97) * mm, "end": v(1.11, 6) * mm});
            skLineSegment(sketch, "E367", {"start": v(1.11, 6) * mm, "end": v(1.09, 6.02) * mm});
            skLineSegment(sketch, "E368", {"start": v(1.09, 6.02) * mm, "end": v(1.06, 6.05) * mm});
            skLineSegment(sketch, "E369", {"start": v(1.06, 6.05) * mm, "end": v(1.05, 6.06) * mm});
            skLineSegment(sketch, "E370", {"start": v(1.05, 6.06) * mm, "end": v(1.03, 6.08) * mm});
            skLineSegment(sketch, "E371", {"start": v(1.03, 6.08) * mm, "end": v(1, 6.1) * mm});
            skLineSegment(sketch, "E372", {"start": v(1, 6.1) * mm, "end": v(0.98, 6.13) * mm});
            skLineSegment(sketch, "E373", {"start": v(0.98, 6.13) * mm, "end": v(0.96, 6.15) * mm});
            skLineSegment(sketch, "E374", {"start": v(0.96, 6.15) * mm, "end": v(0.94, 6.16) * mm});
            skLineSegment(sketch, "E375", {"start": v(0.94, 6.16) * mm, "end": v(0.91, 6.18) * mm});
            skLineSegment(sketch, "E376", {"start": v(0.91, 6.18) * mm, "end": v(0.89, 6.2) * mm});
            skLineSegment(sketch, "E377", {"start": v(0.89, 6.2) * mm, "end": v(0.86, 6.23) * mm});
            skLineSegment(sketch, "E378", {"start": v(0.86, 6.23) * mm, "end": v(0.84, 6.24) * mm});
            skLineSegment(sketch, "E379", {"start": v(0.84, 6.24) * mm, "end": v(0.8, 6.27) * mm});
            skLineSegment(sketch, "E380", {"start": v(0.8, 6.27) * mm, "end": v(0.77, 6.3) * mm});
            skLineSegment(sketch, "E381", {"start": v(0.77, 6.3) * mm, "end": v(0.73, 6.32) * mm});
            skLineSegment(sketch, "E382", {"start": v(0.73, 6.32) * mm, "end": v(0.7, 6.34) * mm});
            skLineSegment(sketch, "E383", {"start": v(0.7, 6.34) * mm, "end": v(0.67, 6.36) * mm});
            skLineSegment(sketch, "E384", {"start": v(0.67, 6.36) * mm, "end": v(0.63, 6.39) * mm});
            skLineSegment(sketch, "E385", {"start": v(0.63, 6.39) * mm, "end": v(0.6, 6.4) * mm});
            skLineSegment(sketch, "E386", {"start": v(0.6, 6.4) * mm, "end": v(0.55, 6.44) * mm});
            skLineSegment(sketch, "E387", {"start": v(0.55, 6.44) * mm, "end": v(0.5, 6.46) * mm});
            skLineSegment(sketch, "E388", {"start": v(0.5, 6.46) * mm, "end": v(0.46, 6.49) * mm});
            skLineSegment(sketch, "E389", {"start": v(0.46, 6.49) * mm, "end": v(0.44, 6.5) * mm});
            skLineSegment(sketch, "E390", {"start": v(0.44, 6.5) * mm, "end": v(0.41, 6.5) * mm});
            skLineSegment(sketch, "E391", {"start": v(0.41, 6.5) * mm, "end": v(0.4, 6.52) * mm});
            skLineSegment(sketch, "E392", {"start": v(0.4, 6.52) * mm, "end": v(0.36, 6.53) * mm});
            skLineSegment(sketch, "E393", {"start": v(0.36, 6.53) * mm, "end": v(0.32, 6.55) * mm});
            skLineSegment(sketch, "E394", {"start": v(0.32, 6.55) * mm, "end": v(0.29, 6.56) * mm});
            skLineSegment(sketch, "E395", {"start": v(0.29, 6.56) * mm, "end": v(0.25, 6.57) * mm});
            skLineSegment(sketch, "E396", {"start": v(0.25, 6.57) * mm, "end": v(0.22, 6.59) * mm});
            skLineSegment(sketch, "E397", {"start": v(0.22, 6.59) * mm, "end": v(0.18, 6.6) * mm});
            skLineSegment(sketch, "E398", {"start": v(0.18, 6.6) * mm, "end": v(0.14, 6.61) * mm});
            skLineSegment(sketch, "E399", {"start": v(0.14, 6.61) * mm, "end": v(0.1, 6.63) * mm});
            skLineSegment(sketch, "E400", {"start": v(0.1, 6.63) * mm, "end": v(0.06, 6.64) * mm});
            skLineSegment(sketch, "E401", {"start": v(0.06, 6.64) * mm, "end": v(0.02, 6.66) * mm});
            skLineSegment(sketch, "E402", {"start": v(0.02, 6.66) * mm, "end": v(-0.02, 6.67) * mm});
            skLineSegment(sketch, "E403", {"start": v(-0.02, 6.67) * mm, "end": v(-0.05, 6.68) * mm});
            skLineSegment(sketch, "E404", {"start": v(-0.05, 6.68) * mm, "end": v(-0.08, 6.7) * mm});
            skLineSegment(sketch, "E405", {"start": v(-0.08, 6.7) * mm, "end": v(-0.11, 6.7) * mm});
            skLineSegment(sketch, "E406", {"start": v(-0.11, 6.7) * mm, "end": v(-0.15, 6.7) * mm});
            skLineSegment(sketch, "E407", {"start": v(-0.15, 6.7) * mm, "end": v(-0.2, 6.7) * mm});
            skLineSegment(sketch, "E408", {"start": v(-0.2, 6.7) * mm, "end": v(-0.23, 6.7) * mm});
            skLineSegment(sketch, "E409", {"start": v(-0.23, 6.7) * mm, "end": v(-0.26, 6.68) * mm});
            skLineSegment(sketch, "E410", {"start": v(-0.26, 6.68) * mm, "end": v(-0.28, 6.66) * mm});
            skLineSegment(sketch, "E411", {"start": v(-0.28, 6.66) * mm, "end": v(-0.29, 6.62) * mm});
            skLineSegment(sketch, "E412", {"start": v(-0.29, 6.62) * mm, "end": v(-0.29, 6.6) * mm});
            skLineSegment(sketch, "E413", {"start": v(-0.29, 6.6) * mm, "end": v(-0.28, 6.55) * mm});
            skLineSegment(sketch, "E414", {"start": v(-0.28, 6.55) * mm, "end": v(-0.27, 6.51) * mm});
            skLineSegment(sketch, "E415", {"start": v(-0.27, 6.51) * mm, "end": v(-0.25, 6.48) * mm});
            skLineSegment(sketch, "E416", {"start": v(-0.25, 6.48) * mm, "end": v(-0.24, 6.44) * mm});
            skLineSegment(sketch, "E417", {"start": v(-0.24, 6.44) * mm, "end": v(-0.24, 6.41) * mm});
            skLineSegment(sketch, "E418", {"start": v(-0.24, 6.41) * mm, "end": v(-0.23, 6.38) * mm});
            skLineSegment(sketch, "E419", {"start": v(-0.23, 6.38) * mm, "end": v(-0.22, 6.35) * mm});
            skLineSegment(sketch, "E420", {"start": v(-0.22, 6.35) * mm, "end": v(-0.21, 6.33) * mm});
            skLineSegment(sketch, "E421", {"start": v(-0.21, 6.33) * mm, "end": v(-0.2, 6.29) * mm});
            skLineSegment(sketch, "E422", {"start": v(-0.2, 6.29) * mm, "end": v(-0.2, 6.24) * mm});
            skLineSegment(sketch, "E423", {"start": v(-0.2, 6.24) * mm, "end": v(-0.18, 6.2) * mm});
            skLineSegment(sketch, "E424", {"start": v(-0.18, 6.2) * mm, "end": v(-0.18, 6.16) * mm});
            skLineSegment(sketch, "E425", {"start": v(-0.18, 6.16) * mm, "end": v(-0.17, 6.12) * mm});
            skLineSegment(sketch, "E426", {"start": v(-0.17, 6.12) * mm, "end": v(-0.16, 6.08) * mm});
            skLineSegment(sketch, "E427", {"start": v(-0.16, 6.08) * mm, "end": v(-0.16, 6.04) * mm});
            skLineSegment(sketch, "E428", {"start": v(-0.16, 6.04) * mm, "end": v(-0.16, 6) * mm});
            skLineSegment(sketch, "E429", {"start": v(-0.16, 6) * mm, "end": v(-0.16, 5.95) * mm});
            skLineSegment(sketch, "E430", {"start": v(-0.16, 5.95) * mm, "end": v(-0.16, 5.93) * mm});
            skLineSegment(sketch, "E431", {"start": v(-0.16, 5.93) * mm, "end": v(-0.16, 5.9) * mm});
            skLineSegment(sketch, "E432", {"start": v(-0.16, 5.9) * mm, "end": v(-0.17, 5.87) * mm});
            skLineSegment(sketch, "E433", {"start": v(-0.17, 5.87) * mm, "end": v(-0.18, 5.84) * mm});
            skLineSegment(sketch, "E434", {"start": v(-0.18, 5.84) * mm, "end": v(-0.2, 5.79) * mm});
            skLineSegment(sketch, "E435", {"start": v(-0.2, 5.79) * mm, "end": v(-0.22, 5.76) * mm});
            skLineSegment(sketch, "E436", {"start": v(-0.22, 5.76) * mm, "end": v(-0.23, 5.74) * mm});
            skLineSegment(sketch, "E437", {"start": v(-0.23, 5.74) * mm, "end": v(-0.25, 5.71) * mm});
            skLineSegment(sketch, "E438", {"start": v(-0.25, 5.71) * mm, "end": v(-0.26, 5.68) * mm});
            skLineSegment(sketch, "E439", {"start": v(-0.26, 5.68) * mm, "end": v(-0.29, 5.64) * mm});
            skLineSegment(sketch, "E440", {"start": v(-0.29, 5.64) * mm, "end": v(-0.3, 5.61) * mm});
            skLineSegment(sketch, "E441", {"start": v(-0.3, 5.61) * mm, "end": v(-0.32, 5.58) * mm});
            skLineSegment(sketch, "E442", {"start": v(-0.32, 5.58) * mm, "end": v(-0.33, 5.56) * mm});
            skLineSegment(sketch, "E443", {"start": v(-0.33, 5.56) * mm, "end": v(-0.34, 5.54) * mm});
            skLineSegment(sketch, "E444", {"start": v(-0.34, 5.54) * mm, "end": v(-0.34, 5.52) * mm});
            skLineSegment(sketch, "E445", {"start": v(-0.34, 5.52) * mm, "end": v(-0.35, 5.47) * mm});
            skLineSegment(sketch, "E446", {"start": v(-0.35, 5.47) * mm, "end": v(-0.36, 5.44) * mm});
            skLineSegment(sketch, "E447", {"start": v(-0.36, 5.44) * mm, "end": v(-0.36, 5.4) * mm});
            skLineSegment(sketch, "E448", {"start": v(-0.36, 5.4) * mm, "end": v(-0.35, 5.36) * mm});
            skLineSegment(sketch, "E449", {"start": v(-0.35, 5.36) * mm, "end": v(-0.35, 5.34) * mm});
            skLineSegment(sketch, "E450", {"start": v(-0.35, 5.34) * mm, "end": v(-0.34, 5.3) * mm});
            skLineSegment(sketch, "E451", {"start": v(-0.34, 5.3) * mm, "end": v(-0.33, 5.29) * mm});
            skLineSegment(sketch, "E452", {"start": v(-0.33, 5.29) * mm, "end": v(-0.32, 5.25) * mm});
            skLineSegment(sketch, "E453", {"start": v(-0.32, 5.25) * mm, "end": v(-0.31, 5.21) * mm});
            skLineSegment(sketch, "E454", {"start": v(-0.31, 5.21) * mm, "end": v(-0.3, 5.18) * mm});
            skLineSegment(sketch, "E455", {"start": v(-0.3, 5.18) * mm, "end": v(-0.3, 5.14) * mm});
            skLineSegment(sketch, "E456", {"start": v(-0.3, 5.14) * mm, "end": v(-0.3, 5.12) * mm});
            skLineSegment(sketch, "E457", {"start": v(-0.3, 5.12) * mm, "end": v(-0.3, 5.09) * mm});
            skLineSegment(sketch, "E458", {"start": v(-0.3, 5.09) * mm, "end": v(-0.33, 5.05) * mm});
            skLineSegment(sketch, "E459", {"start": v(-0.33, 5.05) * mm, "end": v(-0.35, 5.02) * mm});
            skLineSegment(sketch, "E460", {"start": v(-0.35, 5.02) * mm, "end": v(-0.38, 5) * mm});
            skLineSegment(sketch, "E461", {"start": v(-0.38, 5) * mm, "end": v(-0.4, 4.97) * mm});
            skLineSegment(sketch, "E462", {"start": v(-0.4, 4.97) * mm, "end": v(-0.44, 4.94) * mm});
            skLineSegment(sketch, "E463", {"start": v(-0.44, 4.94) * mm, "end": v(-0.46, 4.93) * mm});
            skLineSegment(sketch, "E464", {"start": v(-0.46, 4.93) * mm, "end": v(-0.48, 4.92) * mm});
            skLineSegment(sketch, "E465", {"start": v(-0.48, 4.92) * mm, "end": v(-0.51, 4.9) * mm});
            skLineSegment(sketch, "E466", {"start": v(-0.51, 4.9) * mm, "end": v(-0.53, 4.88) * mm});
            skLineSegment(sketch, "E467", {"start": v(-0.53, 4.88) * mm, "end": v(-0.56, 4.86) * mm});
            skLineSegment(sketch, "E468", {"start": v(-0.56, 4.86) * mm, "end": v(-0.6, 4.83) * mm});
            skLineSegment(sketch, "E469", {"start": v(-0.6, 4.83) * mm, "end": v(-0.63, 4.8) * mm});
            skLineSegment(sketch, "E470", {"start": v(-0.63, 4.8) * mm, "end": v(-0.67, 4.77) * mm});
            skLineSegment(sketch, "E471", {"start": v(-0.67, 4.77) * mm, "end": v(-0.7, 4.74) * mm});
            skLineSegment(sketch, "E472", {"start": v(-0.7, 4.74) * mm, "end": v(-0.73, 4.72) * mm});
            skLineSegment(sketch, "E473", {"start": v(-0.73, 4.72) * mm, "end": v(-0.74, 4.7) * mm});
            skLineSegment(sketch, "E474", {"start": v(-0.74, 4.7) * mm, "end": v(-0.76, 4.68) * mm});
            skLineSegment(sketch, "E475", {"start": v(-0.76, 4.68) * mm, "end": v(-0.78, 4.66) * mm});
            skLineSegment(sketch, "E476", {"start": v(-0.78, 4.66) * mm, "end": v(-0.8, 4.64) * mm});
            skLineSegment(sketch, "E477", {"start": v(-0.8, 4.64) * mm, "end": v(-0.82, 4.62) * mm});
            skLineSegment(sketch, "E478", {"start": v(-0.82, 4.62) * mm, "end": v(-0.84, 4.6) * mm});
            skLineSegment(sketch, "E479", {"start": v(-0.84, 4.6) * mm, "end": v(-0.85, 4.58) * mm});
            skLineSegment(sketch, "E480", {"start": v(-0.85, 4.58) * mm, "end": v(-0.87, 4.55) * mm});
            skLineSegment(sketch, "E481", {"start": v(-0.87, 4.55) * mm, "end": v(-0.89, 4.53) * mm});
            skLineSegment(sketch, "E482", {"start": v(-0.89, 4.53) * mm, "end": v(-0.9, 4.5) * mm});
            skLineSegment(sketch, "E483", {"start": v(-0.9, 4.5) * mm, "end": v(-0.92, 4.49) * mm});
            skLineSegment(sketch, "E484", {"start": v(-0.92, 4.49) * mm, "end": v(-0.93, 4.47) * mm});
            skLineSegment(sketch, "E485", {"start": v(-0.93, 4.47) * mm, "end": v(-0.95, 4.45) * mm});
            skLineSegment(sketch, "E486", {"start": v(-0.95, 4.45) * mm, "end": v(-0.97, 4.41) * mm});
            skLineSegment(sketch, "E487", {"start": v(-0.97, 4.41) * mm, "end": v(-1, 4.36) * mm});
            skLineSegment(sketch, "E488", {"start": v(-1, 4.36) * mm, "end": v(-1.04, 4.3) * mm});
            skLineSegment(sketch, "E489", {"start": v(-1.04, 4.3) * mm, "end": v(-1.06, 4.26) * mm});
            skLineSegment(sketch, "E490", {"start": v(-1.06, 4.26) * mm, "end": v(-1.08, 4.23) * mm});
            skLineSegment(sketch, "E491", {"start": v(-1.08, 4.23) * mm, "end": v(-1.1, 4.2) * mm});
            skLineSegment(sketch, "E492", {"start": v(-1.1, 4.2) * mm, "end": v(-1.1, 4.18) * mm});
            skLineSegment(sketch, "E493", {"start": v(-1.1, 4.18) * mm, "end": v(-1.13, 4.13) * mm});
            skLineSegment(sketch, "E494", {"start": v(-1.13, 4.13) * mm, "end": v(-1.16, 4.09) * mm});
            skLineSegment(sketch, "E495", {"start": v(-1.16, 4.09) * mm, "end": v(-1.18, 4.05) * mm});
            skLineSegment(sketch, "E496", {"start": v(-1.18, 4.05) * mm, "end": v(-1.2, 4) * mm});
            skLineSegment(sketch, "E497", {"start": v(-1.2, 4) * mm, "end": v(-1.2, 3.98) * mm});
            skLineSegment(sketch, "E498", {"start": v(-1.2, 3.98) * mm, "end": v(-1.23, 3.94) * mm});
            skLineSegment(sketch, "E499", {"start": v(-1.23, 3.94) * mm, "end": v(-1.25, 3.9) * mm});
            skLineSegment(sketch, "E500", {"start": v(-1.25, 3.9) * mm, "end": v(-1.26, 3.85) * mm});
            skLineSegment(sketch, "E501", {"start": v(-1.26, 3.85) * mm, "end": v(-1.29, 3.8) * mm});
            skLineSegment(sketch, "E502", {"start": v(-1.29, 3.8) * mm, "end": v(-1.3, 3.76) * mm});
            skLineSegment(sketch, "E503", {"start": v(-1.3, 3.76) * mm, "end": v(-1.32, 3.72) * mm});
            skLineSegment(sketch, "E504", {"start": v(-1.32, 3.72) * mm, "end": v(-1.33, 3.69) * mm});
            skLineSegment(sketch, "E505", {"start": v(-1.33, 3.69) * mm, "end": v(-1.34, 3.65) * mm});
            skLineSegment(sketch, "E506", {"start": v(-1.34, 3.65) * mm, "end": v(-1.35, 3.62) * mm});
            skLineSegment(sketch, "E507", {"start": v(-1.35, 3.62) * mm, "end": v(-1.36, 3.59) * mm});
            skLineSegment(sketch, "E508", {"start": v(-1.36, 3.59) * mm, "end": v(-1.36, 3.56) * mm});
            skLineSegment(sketch, "E509", {"start": v(-1.36, 3.56) * mm, "end": v(-1.37, 3.54) * mm});
            skLineSegment(sketch, "E510", {"start": v(-1.37, 3.54) * mm, "end": v(-1.38, 3.5) * mm});
            skLineSegment(sketch, "E511", {"start": v(-1.38, 3.5) * mm, "end": v(-1.4, 3.46) * mm});
            skLineSegment(sketch, "E512", {"start": v(-1.4, 3.46) * mm, "end": v(-1.41, 3.44) * mm});
            skLineSegment(sketch, "E513", {"start": v(-1.41, 3.44) * mm, "end": v(-1.45, 3.42) * mm});
            skLineSegment(sketch, "E514", {"start": v(-1.45, 3.42) * mm, "end": v(-1.5, 3.4) * mm});
            skLineSegment(sketch, "E515", {"start": v(-1.5, 3.4) * mm, "end": v(-1.52, 3.4) * mm});
            skLineSegment(sketch, "E516", {"start": v(-1.52, 3.4) * mm, "end": v(-1.58, 3.4) * mm});
            skLineSegment(sketch, "E517", {"start": v(-1.58, 3.4) * mm, "end": v(-1.63, 3.39) * mm});
            skLineSegment(sketch, "E518", {"start": v(-1.63, 3.39) * mm, "end": v(-1.67, 3.38) * mm});
            skLineSegment(sketch, "E519", {"start": v(-1.67, 3.38) * mm, "end": v(-1.7, 3.37) * mm});
            skLineSegment(sketch, "E520", {"start": v(-1.7, 3.37) * mm, "end": v(-1.73, 3.37) * mm});
            skLineSegment(sketch, "E521", {"start": v(-1.73, 3.37) * mm, "end": v(-1.78, 3.35) * mm});
            skLineSegment(sketch, "E522", {"start": v(-1.78, 3.35) * mm, "end": v(-1.82, 3.34) * mm});
            skLineSegment(sketch, "E523", {"start": v(-1.82, 3.34) * mm, "end": v(-1.85, 3.32) * mm});
            skLineSegment(sketch, "E524", {"start": v(-1.85, 3.32) * mm, "end": v(-1.89, 3.3) * mm});
            skLineSegment(sketch, "E525", {"start": v(-1.89, 3.3) * mm, "end": v(-1.91, 3.29) * mm});
            skLineSegment(sketch, "E526", {"start": v(-1.91, 3.29) * mm, "end": v(-1.94, 3.27) * mm});
            skLineSegment(sketch, "E527", {"start": v(-1.94, 3.27) * mm, "end": v(-1.96, 3.25) * mm});
            skLineSegment(sketch, "E528", {"start": v(-1.96, 3.25) * mm, "end": v(-1.98, 3.23) * mm});
            skLineSegment(sketch, "E529", {"start": v(-1.98, 3.23) * mm, "end": v(-2, 3.2) * mm});
            skLineSegment(sketch, "E530", {"start": v(-2, 3.2) * mm, "end": v(-2.03, 3.18) * mm});
            skLineSegment(sketch, "E531", {"start": v(-2.03, 3.18) * mm, "end": v(-2.04, 3.17) * mm});
            skLineSegment(sketch, "E532", {"start": v(-2.04, 3.17) * mm, "end": v(-2.06, 3.14) * mm});
            skLineSegment(sketch, "E533", {"start": v(-2.06, 3.14) * mm, "end": v(-2.08, 3.12) * mm});
            skLineSegment(sketch, "E534", {"start": v(-2.08, 3.12) * mm, "end": v(-2.1, 3.08) * mm});
            skLineSegment(sketch, "E535", {"start": v(-2.1, 3.08) * mm, "end": v(-2.13, 3.05) * mm});
            skLineSegment(sketch, "E536", {"start": v(-2.13, 3.05) * mm, "end": v(-2.15, 3.02) * mm});
            skLineSegment(sketch, "E537", {"start": v(-2.15, 3.02) * mm, "end": v(-2.16, 3) * mm});
            skLineSegment(sketch, "E538", {"start": v(-2.16, 3) * mm, "end": v(-2.17, 2.97) * mm});
            skLineSegment(sketch, "E539", {"start": v(-2.17, 2.97) * mm, "end": v(-2.19, 2.94) * mm});
            skLineSegment(sketch, "E540", {"start": v(-2.19, 2.94) * mm, "end": v(-2.2, 2.91) * mm});
            skLineSegment(sketch, "E541", {"start": v(-2.2, 2.91) * mm, "end": v(-2.22, 2.88) * mm});
            skLineSegment(sketch, "E542", {"start": v(-2.22, 2.88) * mm, "end": v(-2.23, 2.85) * mm});
            skLineSegment(sketch, "E543", {"start": v(-2.23, 2.85) * mm, "end": v(-2.24, 2.81) * mm});
            skLineSegment(sketch, "E544", {"start": v(-2.24, 2.81) * mm, "end": v(-2.25, 2.8) * mm});
            skLineSegment(sketch, "E545", {"start": v(-2.25, 2.8) * mm, "end": v(-2.26, 2.77) * mm});
            skLineSegment(sketch, "E546", {"start": v(-2.26, 2.77) * mm, "end": v(-2.26, 2.74) * mm});
            skLineSegment(sketch, "E547", {"start": v(-2.26, 2.74) * mm, "end": v(-2.27, 2.7) * mm});
            skLineSegment(sketch, "E548", {"start": v(-2.27, 2.7) * mm, "end": v(-2.28, 2.67) * mm});
            skLineSegment(sketch, "E549", {"start": v(-2.28, 2.67) * mm, "end": v(-2.28, 2.64) * mm});
            skLineSegment(sketch, "E550", {"start": v(-2.28, 2.64) * mm, "end": v(-2.29, 2.6) * mm});
            skLineSegment(sketch, "E551", {"start": v(-2.29, 2.6) * mm, "end": v(-2.29, 2.56) * mm});
            skLineSegment(sketch, "E552", {"start": v(-2.29, 2.56) * mm, "end": v(-2.29, 2.53) * mm});
            skLineSegment(sketch, "E553", {"start": v(-2.29, 2.53) * mm, "end": v(-2.28, 2.5) * mm});
            skLineSegment(sketch, "E554", {"start": v(-2.28, 2.5) * mm, "end": v(-2.28, 2.46) * mm});
            skLineSegment(sketch, "E555", {"start": v(-2.28, 2.46) * mm, "end": v(-2.27, 2.42) * mm});
            skLineSegment(sketch, "E556", {"start": v(-2.27, 2.42) * mm, "end": v(-2.26, 2.38) * mm});
            skLineSegment(sketch, "E557", {"start": v(-2.26, 2.38) * mm, "end": v(-2.25, 2.34) * mm});
            skLineSegment(sketch, "E558", {"start": v(-2.25, 2.34) * mm, "end": v(-2.24, 2.3) * mm});
            skLineSegment(sketch, "E559", {"start": v(-2.24, 2.3) * mm, "end": v(-2.23, 2.27) * mm});
            skLineSegment(sketch, "E560", {"start": v(-2.23, 2.27) * mm, "end": v(-2.23, 2.23) * mm});
            skLineSegment(sketch, "E561", {"start": v(-2.23, 2.23) * mm, "end": v(-2.22, 2.19) * mm});
            skLineSegment(sketch, "E562", {"start": v(-2.22, 2.19) * mm, "end": v(-2.21, 2.15) * mm});
            skLineSegment(sketch, "E563", {"start": v(-2.21, 2.15) * mm, "end": v(-2.21, 2.11) * mm});
            skLineSegment(sketch, "E564", {"start": v(-2.21, 2.11) * mm, "end": v(-2.21, 2.09) * mm});
            skLineSegment(sketch, "E565", {"start": v(-2.21, 2.09) * mm, "end": v(-2.22, 2.06) * mm});
            skLineSegment(sketch, "E566", {"start": v(-2.22, 2.06) * mm, "end": v(-2.23, 2.04) * mm});
            skLineSegment(sketch, "E567", {"start": v(-2.23, 2.04) * mm, "end": v(-2.24, 2) * mm});
            skLineSegment(sketch, "E568", {"start": v(-2.24, 2) * mm, "end": v(-2.26, 1.99) * mm});
            skLineSegment(sketch, "E569", {"start": v(-2.26, 1.99) * mm, "end": v(-2.29, 1.97) * mm});
            skLineSegment(sketch, "E570", {"start": v(-2.29, 1.97) * mm, "end": v(-2.31, 1.95) * mm});
            skLineSegment(sketch, "E571", {"start": v(-2.31, 1.95) * mm, "end": v(-2.33, 1.94) * mm});
            skLineSegment(sketch, "E572", {"start": v(-2.33, 1.94) * mm, "end": v(-2.36, 1.92) * mm});
            skLineSegment(sketch, "E573", {"start": v(-2.36, 1.92) * mm, "end": v(-2.4, 1.9) * mm});
            skLineSegment(sketch, "E574", {"start": v(-2.4, 1.9) * mm, "end": v(-2.41, 1.88) * mm});
            skLineSegment(sketch, "E575", {"start": v(-2.41, 1.88) * mm, "end": v(-2.43, 1.87) * mm});
            skLineSegment(sketch, "E576", {"start": v(-2.43, 1.87) * mm, "end": v(-2.48, 1.84) * mm});
            skLineSegment(sketch, "E577", {"start": v(-2.48, 1.84) * mm, "end": v(-2.52, 1.81) * mm});
            skLineSegment(sketch, "E578", {"start": v(-2.52, 1.81) * mm, "end": v(-2.54, 1.8) * mm});
            skLineSegment(sketch, "E579", {"start": v(-2.54, 1.8) * mm, "end": v(-2.56, 1.79) * mm});
            skLineSegment(sketch, "E580", {"start": v(-2.56, 1.79) * mm, "end": v(-2.58, 1.78) * mm});
            skLineSegment(sketch, "E581", {"start": v(-2.58, 1.78) * mm, "end": v(-2.6, 1.76) * mm});
            skLineSegment(sketch, "E582", {"start": v(-2.6, 1.76) * mm, "end": v(-2.64, 1.74) * mm});
            skLineSegment(sketch, "E583", {"start": v(-2.64, 1.74) * mm, "end": v(-2.66, 1.72) * mm});
            skLineSegment(sketch, "E584", {"start": v(-2.66, 1.72) * mm, "end": v(-2.7, 1.69) * mm});
            skLineSegment(sketch, "E585", {"start": v(-2.7, 1.69) * mm, "end": v(-2.76, 1.64) * mm});
            skLineSegment(sketch, "E586", {"start": v(-2.76, 1.64) * mm, "end": v(-2.8, 1.6) * mm});
            skLineSegment(sketch, "E587", {"start": v(-2.8, 1.6) * mm, "end": v(-2.84, 1.56) * mm});
            skLineSegment(sketch, "E588", {"start": v(-2.84, 1.56) * mm, "end": v(-2.86, 1.52) * mm});
            skLineSegment(sketch, "E589", {"start": v(-2.86, 1.52) * mm, "end": v(-2.89, 1.48) * mm});
            skLineSegment(sketch, "E590", {"start": v(-2.89, 1.48) * mm, "end": v(-2.9, 1.44) * mm});
            skLineSegment(sketch, "E591", {"start": v(-2.9, 1.44) * mm, "end": v(-2.93, 1.4) * mm});
            skLineSegment(sketch, "E592", {"start": v(-2.93, 1.4) * mm, "end": v(-2.95, 1.37) * mm});
            skLineSegment(sketch, "E593", {"start": v(-2.95, 1.37) * mm, "end": v(-2.96, 1.33) * mm});
            skLineSegment(sketch, "E594", {"start": v(-2.96, 1.33) * mm, "end": v(-2.98, 1.3) * mm});
            skLineSegment(sketch, "E595", {"start": v(-2.98, 1.3) * mm, "end": v(-3, 1.26) * mm});
            skLineSegment(sketch, "E596", {"start": v(-3, 1.26) * mm, "end": v(-3, 1.23) * mm});
            skLineSegment(sketch, "E597", {"start": v(-3, 1.23) * mm, "end": v(-3.02, 1.2) * mm});
            skLineSegment(sketch, "E598", {"start": v(-3.02, 1.2) * mm, "end": v(-3.04, 1.16) * mm});
            skLineSegment(sketch, "E599", {"start": v(-3.04, 1.16) * mm, "end": v(-3.05, 1.12) * mm});
            skLineSegment(sketch, "E600", {"start": v(-3.05, 1.12) * mm, "end": v(-3.06, 1.09) * mm});
            skLineSegment(sketch, "E601", {"start": v(-3.06, 1.09) * mm, "end": v(-3.08, 1.05) * mm});
            skLineSegment(sketch, "E602", {"start": v(-3.08, 1.05) * mm, "end": v(-3.1, 1.01) * mm});
            skLineSegment(sketch, "E603", {"start": v(-3.1, 1.01) * mm, "end": v(-3.1, 0.97) * mm});
            skLineSegment(sketch, "E604", {"start": v(-3.1, 0.97) * mm, "end": v(-3.12, 0.93) * mm});
            skLineSegment(sketch, "E605", {"start": v(-3.12, 0.93) * mm, "end": v(-3.13, 0.9) * mm});
            skLineSegment(sketch, "E606", {"start": v(-3.13, 0.9) * mm, "end": v(-3.14, 0.86) * mm});
            skLineSegment(sketch, "E607", {"start": v(-3.14, 0.86) * mm, "end": v(-3.15, 0.82) * mm});
            skLineSegment(sketch, "E608", {"start": v(-3.15, 0.82) * mm, "end": v(-3.16, 0.79) * mm});
            skLineSegment(sketch, "E609", {"start": v(-3.16, 0.79) * mm, "end": v(-3.17, 0.77) * mm});
            skLineSegment(sketch, "E610", {"start": v(-3.17, 0.77) * mm, "end": v(-3.17, 0.73) * mm});
            skLineSegment(sketch, "E611", {"start": v(-3.17, 0.73) * mm, "end": v(-3.18, 0.69) * mm});
            skLineSegment(sketch, "E612", {"start": v(-3.18, 0.69) * mm, "end": v(-3.18, 0.65) * mm});
            skLineSegment(sketch, "E613", {"start": v(-3.18, 0.65) * mm, "end": v(-3.18, 0.61) * mm});
            skLineSegment(sketch, "E614", {"start": v(-3.18, 0.61) * mm, "end": v(-3.18, 0.57) * mm});
            skLineSegment(sketch, "E615", {"start": v(-3.18, 0.57) * mm, "end": v(-3.18, 0.54) * mm});
            skLineSegment(sketch, "E616", {"start": v(-3.18, 0.54) * mm, "end": v(-3.18, 0.5) * mm});
            skLineSegment(sketch, "E617", {"start": v(-3.18, 0.5) * mm, "end": v(-3.18, 0.46) * mm});
            skLineSegment(sketch, "E618", {"start": v(-3.18, 0.46) * mm, "end": v(-3.17, 0.42) * mm});
            skLineSegment(sketch, "E619", {"start": v(-3.17, 0.42) * mm, "end": v(-3.17, 0.4) * mm});
            skLineSegment(sketch, "E620", {"start": v(-3.17, 0.4) * mm, "end": v(-3.16, 0.36) * mm});
            skLineSegment(sketch, "E621", {"start": v(-3.16, 0.36) * mm, "end": v(-3.16, 0.31) * mm});
            skLineSegment(sketch, "E622", {"start": v(-3.16, 0.31) * mm, "end": v(-3.16, 0.28) * mm});
            skLineSegment(sketch, "E623", {"start": v(-3.16, 0.28) * mm, "end": v(-3.16, 0.26) * mm});
            skLineSegment(sketch, "E624", {"start": v(-3.16, 0.26) * mm, "end": v(-3.15, 0.2) * mm});
            skLineSegment(sketch, "E625", {"start": v(-3.15, 0.2) * mm, "end": v(-3.14, 0.19) * mm});
            skSolve(sketch);
        }
        {
            var Q0;
            Q0 = qSketchRegion(id + "F0", true);
            extrude(context, id + "F1", {"entities" : qUnion([Q0]), "oppositeDirection" : true, "depth" : 0.1 * mm, "offsetDistance" : 25 * mm});
        }
        {
            var Q0;
            Q0=makeQuery(id+"F1.opExtrude","SWEPT_BODY",BODY,{"disambiguationData":[OSD([sQuery(id+"F0.wireOp",EDGE,"E0"),sQuery(id+"F0.wireOp",EDGE,"E1"),sQuery(id+"F0.wireOp",EDGE,"E2"),sQuery(id+"F0.wireOp",EDGE,"E3"),sQuery(id+"F0.wireOp",EDGE,"E4"),sQuery(id+"F0.wireOp",EDGE,"E5"),sQuery(id+"F0.wireOp",EDGE,"E6"),sQuery(id+"F0.wireOp",EDGE,"E7"),sQuery(id+"F0.wireOp",EDGE,"E8"),sQuery(id+"F0.wireOp",EDGE,"E9"),sQuery(id+"F0.wireOp",EDGE,"E10"),sQuery(id+"F0.wireOp",EDGE,"E11"),sQuery(id+"F0.wireOp",EDGE,"E12"),sQuery(id+"F0.wireOp",EDGE,"E13"),sQuery(id+"F0.wireOp",EDGE,"E14"),sQuery(id+"F0.wireOp",EDGE,"E15"),sQuery(id+"F0.wireOp",EDGE,"E16"),sQuery(id+"F0.wireOp",EDGE,"E17"),sQuery(id+"F0.wireOp",EDGE,"E18"),sQuery(id+"F0.wireOp",EDGE,"E19"),sQuery(id+"F0.wireOp",EDGE,"E20"),sQuery(id+"F0.wireOp",EDGE,"E21"),sQuery(id+"F0.wireOp",EDGE,"E22"),sQuery(id+"F0.wireOp",EDGE,"E23"),sQuery(id+"F0.wireOp",EDGE,"E24"),sQuery(id+"F0.wireOp",EDGE,"E25"),sQuery(id+"F0.wireOp",EDGE,"E26"),sQuery(id+"F0.wireOp",EDGE,"E27"),sQuery(id+"F0.wireOp",EDGE,"E28"),sQuery(id+"F0.wireOp",EDGE,"E29"),sQuery(id+"F0.wireOp",EDGE,"E30"),sQuery(id+"F0.wireOp",EDGE,"E31"),sQuery(id+"F0.wireOp",EDGE,"E32"),sQuery(id+"F0.wireOp",EDGE,"E33"),sQuery(id+"F0.wireOp",EDGE,"E34"),sQuery(id+"F0.wireOp",EDGE,"E35"),sQuery(id+"F0.wireOp",EDGE,"E36"),sQuery(id+"F0.wireOp",EDGE,"E37"),sQuery(id+"F0.wireOp",EDGE,"E38"),sQuery(id+"F0.wireOp",EDGE,"E39"),sQuery(id+"F0.wireOp",EDGE,"E40"),sQuery(id+"F0.wireOp",EDGE,"E41"),sQuery(id+"F0.wireOp",EDGE,"E42"),sQuery(id+"F0.wireOp",EDGE,"E43"),sQuery(id+"F0.wireOp",EDGE,"E44"),sQuery(id+"F0.wireOp",EDGE,"E45"),sQuery(id+"F0.wireOp",EDGE,"E46"),sQuery(id+"F0.wireOp",EDGE,"E47"),sQuery(id+"F0.wireOp",EDGE,"E48"),sQuery(id+"F0.wireOp",EDGE,"E49"),sQuery(id+"F0.wireOp",EDGE,"E50"),sQuery(id+"F0.wireOp",EDGE,"E51"),sQuery(id+"F0.wireOp",EDGE,"E52"),sQuery(id+"F0.wireOp",EDGE,"E53"),sQuery(id+"F0.wireOp",EDGE,"E54"),sQuery(id+"F0.wireOp",EDGE,"E55"),sQuery(id+"F0.wireOp",EDGE,"E56"),sQuery(id+"F0.wireOp",EDGE,"E57"),sQuery(id+"F0.wireOp",EDGE,"E58"),sQuery(id+"F0.wireOp",EDGE,"E59"),sQuery(id+"F0.wireOp",EDGE,"E60"),sQuery(id+"F0.wireOp",EDGE,"E61"),sQuery(id+"F0.wireOp",EDGE,"E62"),sQuery(id+"F0.wireOp",EDGE,"E63"),sQuery(id+"F0.wireOp",EDGE,"E64"),sQuery(id+"F0.wireOp",EDGE,"E65"),sQuery(id+"F0.wireOp",EDGE,"E66"),sQuery(id+"F0.wireOp",EDGE,"E67"),sQuery(id+"F0.wireOp",EDGE,"E68"),sQuery(id+"F0.wireOp",EDGE,"E69"),sQuery(id+"F0.wireOp",EDGE,"E70"),sQuery(id+"F0.wireOp",EDGE,"E71"),sQuery(id+"F0.wireOp",EDGE,"E72"),sQuery(id+"F0.wireOp",EDGE,"E73"),sQuery(id+"F0.wireOp",EDGE,"E74"),sQuery(id+"F0.wireOp",EDGE,"E75"),sQuery(id+"F0.wireOp",EDGE,"E76"),sQuery(id+"F0.wireOp",EDGE,"E77"),sQuery(id+"F0.wireOp",EDGE,"E78"),sQuery(id+"F0.wireOp",EDGE,"E79"),sQuery(id+"F0.wireOp",EDGE,"E80"),sQuery(id+"F0.wireOp",EDGE,"E81"),sQuery(id+"F0.wireOp",EDGE,"E82"),sQuery(id+"F0.wireOp",EDGE,"E83"),sQuery(id+"F0.wireOp",EDGE,"E84"),sQuery(id+"F0.wireOp",EDGE,"E85"),sQuery(id+"F0.wireOp",EDGE,"E86"),sQuery(id+"F0.wireOp",EDGE,"E87"),sQuery(id+"F0.wireOp",EDGE,"E88"),sQuery(id+"F0.wireOp",EDGE,"E89"),sQuery(id+"F0.wireOp",EDGE,"E90"),sQuery(id+"F0.wireOp",EDGE,"E91"),sQuery(id+"F0.wireOp",EDGE,"E92"),sQuery(id+"F0.wireOp",EDGE,"E93"),sQuery(id+"F0.wireOp",EDGE,"E94"),sQuery(id+"F0.wireOp",EDGE,"E95"),sQuery(id+"F0.wireOp",EDGE,"E96"),sQuery(id+"F0.wireOp",EDGE,"E97"),sQuery(id+"F0.wireOp",EDGE,"E98"),sQuery(id+"F0.wireOp",EDGE,"E99"),sQuery(id+"F0.wireOp",EDGE,"E100"),sQuery(id+"F0.wireOp",EDGE,"E101"),sQuery(id+"F0.wireOp",EDGE,"E102"),sQuery(id+"F0.wireOp",EDGE,"E103"),sQuery(id+"F0.wireOp",EDGE,"E104"),sQuery(id+"F0.wireOp",EDGE,"E105"),sQuery(id+"F0.wireOp",EDGE,"E106"),sQuery(id+"F0.wireOp",EDGE,"E107"),sQuery(id+"F0.wireOp",EDGE,"E108"),sQuery(id+"F0.wireOp",EDGE,"E109"),sQuery(id+"F0.wireOp",EDGE,"E110"),sQuery(id+"F0.wireOp",EDGE,"E111"),sQuery(id+"F0.wireOp",EDGE,"E112"),sQuery(id+"F0.wireOp",EDGE,"E113"),sQuery(id+"F0.wireOp",EDGE,"E114"),sQuery(id+"F0.wireOp",EDGE,"E115"),sQuery(id+"F0.wireOp",EDGE,"E116"),sQuery(id+"F0.wireOp",EDGE,"E117"),sQuery(id+"F0.wireOp",EDGE,"E118"),sQuery(id+"F0.wireOp",EDGE,"E119"),sQuery(id+"F0.wireOp",EDGE,"E120"),sQuery(id+"F0.wireOp",EDGE,"E121"),sQuery(id+"F0.wireOp",EDGE,"E122"),sQuery(id+"F0.wireOp",EDGE,"E123"),sQuery(id+"F0.wireOp",EDGE,"E124"),sQuery(id+"F0.wireOp",EDGE,"E125"),sQuery(id+"F0.wireOp",EDGE,"E126"),sQuery(id+"F0.wireOp",EDGE,"E127"),sQuery(id+"F0.wireOp",EDGE,"E128"),sQuery(id+"F0.wireOp",EDGE,"E129"),sQuery(id+"F0.wireOp",EDGE,"E130"),sQuery(id+"F0.wireOp",EDGE,"E131"),sQuery(id+"F0.wireOp",EDGE,"E132"),sQuery(id+"F0.wireOp",EDGE,"E133"),sQuery(id+"F0.wireOp",EDGE,"E134"),sQuery(id+"F0.wireOp",EDGE,"E135"),sQuery(id+"F0.wireOp",EDGE,"E136"),sQuery(id+"F0.wireOp",EDGE,"E137"),sQuery(id+"F0.wireOp",EDGE,"E138"),sQuery(id+"F0.wireOp",EDGE,"E139"),sQuery(id+"F0.wireOp",EDGE,"E140"),sQuery(id+"F0.wireOp",EDGE,"E141"),sQuery(id+"F0.wireOp",EDGE,"E142"),sQuery(id+"F0.wireOp",EDGE,"E143"),sQuery(id+"F0.wireOp",EDGE,"E144"),sQuery(id+"F0.wireOp",EDGE,"E145"),sQuery(id+"F0.wireOp",EDGE,"E146"),sQuery(id+"F0.wireOp",EDGE,"E147"),sQuery(id+"F0.wireOp",EDGE,"E148"),sQuery(id+"F0.wireOp",EDGE,"E149"),sQuery(id+"F0.wireOp",EDGE,"E150"),sQuery(id+"F0.wireOp",EDGE,"E151"),sQuery(id+"F0.wireOp",EDGE,"E152"),sQuery(id+"F0.wireOp",EDGE,"E153"),sQuery(id+"F0.wireOp",EDGE,"E154"),sQuery(id+"F0.wireOp",EDGE,"E155"),sQuery(id+"F0.wireOp",EDGE,"E156"),sQuery(id+"F0.wireOp",EDGE,"E157"),sQuery(id+"F0.wireOp",EDGE,"E158"),sQuery(id+"F0.wireOp",EDGE,"E159"),sQuery(id+"F0.wireOp",EDGE,"E160"),sQuery(id+"F0.wireOp",EDGE,"E161"),sQuery(id+"F0.wireOp",EDGE,"E162"),sQuery(id+"F0.wireOp",EDGE,"E163"),sQuery(id+"F0.wireOp",EDGE,"E164"),sQuery(id+"F0.wireOp",EDGE,"E165"),sQuery(id+"F0.wireOp",EDGE,"E166"),sQuery(id+"F0.wireOp",EDGE,"E167"),sQuery(id+"F0.wireOp",EDGE,"E168"),sQuery(id+"F0.wireOp",EDGE,"E169"),sQuery(id+"F0.wireOp",EDGE,"E170"),sQuery(id+"F0.wireOp",EDGE,"E171"),sQuery(id+"F0.wireOp",EDGE,"E172"),sQuery(id+"F0.wireOp",EDGE,"E173"),sQuery(id+"F0.wireOp",EDGE,"E174"),sQuery(id+"F0.wireOp",EDGE,"E175"),sQuery(id+"F0.wireOp",EDGE,"E176"),sQuery(id+"F0.wireOp",EDGE,"E177"),sQuery(id+"F0.wireOp",EDGE,"E178"),sQuery(id+"F0.wireOp",EDGE,"E179"),sQuery(id+"F0.wireOp",EDGE,"E180"),sQuery(id+"F0.wireOp",EDGE,"E181"),sQuery(id+"F0.wireOp",EDGE,"E182"),sQuery(id+"F0.wireOp",EDGE,"E183"),sQuery(id+"F0.wireOp",EDGE,"E184"),sQuery(id+"F0.wireOp",EDGE,"E185"),sQuery(id+"F0.wireOp",EDGE,"E186"),sQuery(id+"F0.wireOp",EDGE,"E187"),sQuery(id+"F0.wireOp",EDGE,"E188"),sQuery(id+"F0.wireOp",EDGE,"E189"),sQuery(id+"F0.wireOp",EDGE,"E190"),sQuery(id+"F0.wireOp",EDGE,"E191"),sQuery(id+"F0.wireOp",EDGE,"E192"),sQuery(id+"F0.wireOp",EDGE,"E193"),sQuery(id+"F0.wireOp",EDGE,"E194"),sQuery(id+"F0.wireOp",EDGE,"E195"),sQuery(id+"F0.wireOp",EDGE,"E196"),sQuery(id+"F0.wireOp",EDGE,"E197"),sQuery(id+"F0.wireOp",EDGE,"E198"),sQuery(id+"F0.wireOp",EDGE,"E199"),sQuery(id+"F0.wireOp",EDGE,"E200"),sQuery(id+"F0.wireOp",EDGE,"E201"),sQuery(id+"F0.wireOp",EDGE,"E202"),sQuery(id+"F0.wireOp",EDGE,"E203"),sQuery(id+"F0.wireOp",EDGE,"E204"),sQuery(id+"F0.wireOp",EDGE,"E205"),sQuery(id+"F0.wireOp",EDGE,"E206"),sQuery(id+"F0.wireOp",EDGE,"E207"),sQuery(id+"F0.wireOp",EDGE,"E208"),sQuery(id+"F0.wireOp",EDGE,"E209"),sQuery(id+"F0.wireOp",EDGE,"E210"),sQuery(id+"F0.wireOp",EDGE,"E211"),sQuery(id+"F0.wireOp",EDGE,"E212"),sQuery(id+"F0.wireOp",EDGE,"E213"),sQuery(id+"F0.wireOp",EDGE,"E214"),sQuery(id+"F0.wireOp",EDGE,"E215"),sQuery(id+"F0.wireOp",EDGE,"E216"),sQuery(id+"F0.wireOp",EDGE,"E217"),sQuery(id+"F0.wireOp",EDGE,"E218"),sQuery(id+"F0.wireOp",EDGE,"E219"),sQuery(id+"F0.wireOp",EDGE,"E220"),sQuery(id+"F0.wireOp",EDGE,"E221"),sQuery(id+"F0.wireOp",EDGE,"E222"),sQuery(id+"F0.wireOp",EDGE,"E223"),sQuery(id+"F0.wireOp",EDGE,"E224"),sQuery(id+"F0.wireOp",EDGE,"E225"),sQuery(id+"F0.wireOp",EDGE,"E226"),sQuery(id+"F0.wireOp",EDGE,"E227"),sQuery(id+"F0.wireOp",EDGE,"E228"),sQuery(id+"F0.wireOp",EDGE,"E229"),sQuery(id+"F0.wireOp",EDGE,"E230"),sQuery(id+"F0.wireOp",EDGE,"E231"),sQuery(id+"F0.wireOp",EDGE,"E232"),sQuery(id+"F0.wireOp",EDGE,"E233"),sQuery(id+"F0.wireOp",EDGE,"E234"),sQuery(id+"F0.wireOp",EDGE,"E235"),sQuery(id+"F0.wireOp",EDGE,"E236"),sQuery(id+"F0.wireOp",EDGE,"E237"),sQuery(id+"F0.wireOp",EDGE,"E238"),sQuery(id+"F0.wireOp",EDGE,"E239"),sQuery(id+"F0.wireOp",EDGE,"E240"),sQuery(id+"F0.wireOp",EDGE,"E241"),sQuery(id+"F0.wireOp",EDGE,"E242"),sQuery(id+"F0.wireOp",EDGE,"E243"),sQuery(id+"F0.wireOp",EDGE,"E244"),sQuery(id+"F0.wireOp",EDGE,"E245"),sQuery(id+"F0.wireOp",EDGE,"E246"),sQuery(id+"F0.wireOp",EDGE,"E247"),sQuery(id+"F0.wireOp",EDGE,"E248"),sQuery(id+"F0.wireOp",EDGE,"E249"),sQuery(id+"F0.wireOp",EDGE,"E250"),sQuery(id+"F0.wireOp",EDGE,"E251"),sQuery(id+"F0.wireOp",EDGE,"E252"),sQuery(id+"F0.wireOp",EDGE,"E253"),sQuery(id+"F0.wireOp",EDGE,"E254"),sQuery(id+"F0.wireOp",EDGE,"E255"),sQuery(id+"F0.wireOp",EDGE,"E256"),sQuery(id+"F0.wireOp",EDGE,"E257"),sQuery(id+"F0.wireOp",EDGE,"E258"),sQuery(id+"F0.wireOp",EDGE,"E259"),sQuery(id+"F0.wireOp",EDGE,"E260"),sQuery(id+"F0.wireOp",EDGE,"E261"),sQuery(id+"F0.wireOp",EDGE,"E262"),sQuery(id+"F0.wireOp",EDGE,"E263"),sQuery(id+"F0.wireOp",EDGE,"E264"),sQuery(id+"F0.wireOp",EDGE,"E265"),sQuery(id+"F0.wireOp",EDGE,"E266"),sQuery(id+"F0.wireOp",EDGE,"E267"),sQuery(id+"F0.wireOp",EDGE,"E268"),sQuery(id+"F0.wireOp",EDGE,"E269"),sQuery(id+"F0.wireOp",EDGE,"E270"),sQuery(id+"F0.wireOp",EDGE,"E271"),sQuery(id+"F0.wireOp",EDGE,"E272"),sQuery(id+"F0.wireOp",EDGE,"E273"),sQuery(id+"F0.wireOp",EDGE,"E274"),sQuery(id+"F0.wireOp",EDGE,"E275"),sQuery(id+"F0.wireOp",EDGE,"E276"),sQuery(id+"F0.wireOp",EDGE,"E277"),sQuery(id+"F0.wireOp",EDGE,"E278"),sQuery(id+"F0.wireOp",EDGE,"E279"),sQuery(id+"F0.wireOp",EDGE,"E280"),sQuery(id+"F0.wireOp",EDGE,"E281"),sQuery(id+"F0.wireOp",EDGE,"E282"),sQuery(id+"F0.wireOp",EDGE,"E283"),sQuery(id+"F0.wireOp",EDGE,"E284"),sQuery(id+"F0.wireOp",EDGE,"E285"),sQuery(id+"F0.wireOp",EDGE,"E286"),sQuery(id+"F0.wireOp",EDGE,"E287"),sQuery(id+"F0.wireOp",EDGE,"E288"),sQuery(id+"F0.wireOp",EDGE,"E289"),sQuery(id+"F0.wireOp",EDGE,"E290"),sQuery(id+"F0.wireOp",EDGE,"E291"),sQuery(id+"F0.wireOp",EDGE,"E292"),sQuery(id+"F0.wireOp",EDGE,"E293"),sQuery(id+"F0.wireOp",EDGE,"E294"),sQuery(id+"F0.wireOp",EDGE,"E295"),sQuery(id+"F0.wireOp",EDGE,"E296"),sQuery(id+"F0.wireOp",EDGE,"E297"),sQuery(id+"F0.wireOp",EDGE,"E298"),sQuery(id+"F0.wireOp",EDGE,"E299"),sQuery(id+"F0.wireOp",EDGE,"E300"),sQuery(id+"F0.wireOp",EDGE,"E301"),sQuery(id+"F0.wireOp",EDGE,"E302"),sQuery(id+"F0.wireOp",EDGE,"E303"),sQuery(id+"F0.wireOp",EDGE,"E304"),sQuery(id+"F0.wireOp",EDGE,"E305"),sQuery(id+"F0.wireOp",EDGE,"E306"),sQuery(id+"F0.wireOp",EDGE,"E307"),sQuery(id+"F0.wireOp",EDGE,"E308"),sQuery(id+"F0.wireOp",EDGE,"E309"),sQuery(id+"F0.wireOp",EDGE,"E310"),sQuery(id+"F0.wireOp",EDGE,"E311"),sQuery(id+"F0.wireOp",EDGE,"E312"),sQuery(id+"F0.wireOp",EDGE,"E313"),sQuery(id+"F0.wireOp",EDGE,"E314"),sQuery(id+"F0.wireOp",EDGE,"E315"),sQuery(id+"F0.wireOp",EDGE,"E316"),sQuery(id+"F0.wireOp",EDGE,"E317"),sQuery(id+"F0.wireOp",EDGE,"E318"),sQuery(id+"F0.wireOp",EDGE,"E319"),sQuery(id+"F0.wireOp",EDGE,"E320"),sQuery(id+"F0.wireOp",EDGE,"E321"),sQuery(id+"F0.wireOp",EDGE,"E322"),sQuery(id+"F0.wireOp",EDGE,"E323"),sQuery(id+"F0.wireOp",EDGE,"E324"),sQuery(id+"F0.wireOp",EDGE,"E325"),sQuery(id+"F0.wireOp",EDGE,"E326"),sQuery(id+"F0.wireOp",EDGE,"E327"),sQuery(id+"F0.wireOp",EDGE,"E328"),sQuery(id+"F0.wireOp",EDGE,"E329"),sQuery(id+"F0.wireOp",EDGE,"E330"),sQuery(id+"F0.wireOp",EDGE,"E331"),sQuery(id+"F0.wireOp",EDGE,"E332"),sQuery(id+"F0.wireOp",EDGE,"E333"),sQuery(id+"F0.wireOp",EDGE,"E334"),sQuery(id+"F0.wireOp",EDGE,"E335"),sQuery(id+"F0.wireOp",EDGE,"E336"),sQuery(id+"F0.wireOp",EDGE,"E337"),sQuery(id+"F0.wireOp",EDGE,"E338"),sQuery(id+"F0.wireOp",EDGE,"E339"),sQuery(id+"F0.wireOp",EDGE,"E340"),sQuery(id+"F0.wireOp",EDGE,"E341"),sQuery(id+"F0.wireOp",EDGE,"E342"),sQuery(id+"F0.wireOp",EDGE,"E343"),sQuery(id+"F0.wireOp",EDGE,"E344"),sQuery(id+"F0.wireOp",EDGE,"E345"),sQuery(id+"F0.wireOp",EDGE,"E346"),sQuery(id+"F0.wireOp",EDGE,"E347"),sQuery(id+"F0.wireOp",EDGE,"E348"),sQuery(id+"F0.wireOp",EDGE,"E349"),sQuery(id+"F0.wireOp",EDGE,"E350"),sQuery(id+"F0.wireOp",EDGE,"E351"),sQuery(id+"F0.wireOp",EDGE,"E352"),sQuery(id+"F0.wireOp",EDGE,"E353"),sQuery(id+"F0.wireOp",EDGE,"E354"),sQuery(id+"F0.wireOp",EDGE,"E355"),sQuery(id+"F0.wireOp",EDGE,"E356"),sQuery(id+"F0.wireOp",EDGE,"E357"),sQuery(id+"F0.wireOp",EDGE,"E358"),sQuery(id+"F0.wireOp",EDGE,"E359"),sQuery(id+"F0.wireOp",EDGE,"E360"),sQuery(id+"F0.wireOp",EDGE,"E361"),sQuery(id+"F0.wireOp",EDGE,"E362"),sQuery(id+"F0.wireOp",EDGE,"E363"),sQuery(id+"F0.wireOp",EDGE,"E364"),sQuery(id+"F0.wireOp",EDGE,"E365"),sQuery(id+"F0.wireOp",EDGE,"E366"),sQuery(id+"F0.wireOp",EDGE,"E367"),sQuery(id+"F0.wireOp",EDGE,"E368"),sQuery(id+"F0.wireOp",EDGE,"E369"),sQuery(id+"F0.wireOp",EDGE,"E370"),sQuery(id+"F0.wireOp",EDGE,"E371"),sQuery(id+"F0.wireOp",EDGE,"E372"),sQuery(id+"F0.wireOp",EDGE,"E373"),sQuery(id+"F0.wireOp",EDGE,"E374"),sQuery(id+"F0.wireOp",EDGE,"E375"),sQuery(id+"F0.wireOp",EDGE,"E376"),sQuery(id+"F0.wireOp",EDGE,"E377"),sQuery(id+"F0.wireOp",EDGE,"E378"),sQuery(id+"F0.wireOp",EDGE,"E379"),sQuery(id+"F0.wireOp",EDGE,"E380"),sQuery(id+"F0.wireOp",EDGE,"E381"),sQuery(id+"F0.wireOp",EDGE,"E382"),sQuery(id+"F0.wireOp",EDGE,"E383"),sQuery(id+"F0.wireOp",EDGE,"E384"),sQuery(id+"F0.wireOp",EDGE,"E385"),sQuery(id+"F0.wireOp",EDGE,"E386"),sQuery(id+"F0.wireOp",EDGE,"E387"),sQuery(id+"F0.wireOp",EDGE,"E388"),sQuery(id+"F0.wireOp",EDGE,"E389"),sQuery(id+"F0.wireOp",EDGE,"E390"),sQuery(id+"F0.wireOp",EDGE,"E391"),sQuery(id+"F0.wireOp",EDGE,"E392"),sQuery(id+"F0.wireOp",EDGE,"E393"),sQuery(id+"F0.wireOp",EDGE,"E394"),sQuery(id+"F0.wireOp",EDGE,"E395"),sQuery(id+"F0.wireOp",EDGE,"E396"),sQuery(id+"F0.wireOp",EDGE,"E397"),sQuery(id+"F0.wireOp",EDGE,"E398"),sQuery(id+"F0.wireOp",EDGE,"E399"),sQuery(id+"F0.wireOp",EDGE,"E400"),sQuery(id+"F0.wireOp",EDGE,"E401"),sQuery(id+"F0.wireOp",EDGE,"E402"),sQuery(id+"F0.wireOp",EDGE,"E403"),sQuery(id+"F0.wireOp",EDGE,"E404"),sQuery(id+"F0.wireOp",EDGE,"E405"),sQuery(id+"F0.wireOp",EDGE,"E406"),sQuery(id+"F0.wireOp",EDGE,"E407"),sQuery(id+"F0.wireOp",EDGE,"E408"),sQuery(id+"F0.wireOp",EDGE,"E409"),sQuery(id+"F0.wireOp",EDGE,"E410"),sQuery(id+"F0.wireOp",EDGE,"E411"),sQuery(id+"F0.wireOp",EDGE,"E412"),sQuery(id+"F0.wireOp",EDGE,"E413"),sQuery(id+"F0.wireOp",EDGE,"E414"),sQuery(id+"F0.wireOp",EDGE,"E415"),sQuery(id+"F0.wireOp",EDGE,"E416"),sQuery(id+"F0.wireOp",EDGE,"E417"),sQuery(id+"F0.wireOp",EDGE,"E418"),sQuery(id+"F0.wireOp",EDGE,"E419"),sQuery(id+"F0.wireOp",EDGE,"E420"),sQuery(id+"F0.wireOp",EDGE,"E421"),sQuery(id+"F0.wireOp",EDGE,"E422"),sQuery(id+"F0.wireOp",EDGE,"E423"),sQuery(id+"F0.wireOp",EDGE,"E424"),sQuery(id+"F0.wireOp",EDGE,"E425"),sQuery(id+"F0.wireOp",EDGE,"E426"),sQuery(id+"F0.wireOp",EDGE,"E427"),sQuery(id+"F0.wireOp",EDGE,"E428"),sQuery(id+"F0.wireOp",EDGE,"E429"),sQuery(id+"F0.wireOp",EDGE,"E430"),sQuery(id+"F0.wireOp",EDGE,"E431"),sQuery(id+"F0.wireOp",EDGE,"E432"),sQuery(id+"F0.wireOp",EDGE,"E433"),sQuery(id+"F0.wireOp",EDGE,"E434"),sQuery(id+"F0.wireOp",EDGE,"E435"),sQuery(id+"F0.wireOp",EDGE,"E436"),sQuery(id+"F0.wireOp",EDGE,"E437"),sQuery(id+"F0.wireOp",EDGE,"E438"),sQuery(id+"F0.wireOp",EDGE,"E439"),sQuery(id+"F0.wireOp",EDGE,"E440"),sQuery(id+"F0.wireOp",EDGE,"E441"),sQuery(id+"F0.wireOp",EDGE,"E442"),sQuery(id+"F0.wireOp",EDGE,"E443"),sQuery(id+"F0.wireOp",EDGE,"E444"),sQuery(id+"F0.wireOp",EDGE,"E445"),sQuery(id+"F0.wireOp",EDGE,"E446"),sQuery(id+"F0.wireOp",EDGE,"E447"),sQuery(id+"F0.wireOp",EDGE,"E448"),sQuery(id+"F0.wireOp",EDGE,"E449"),sQuery(id+"F0.wireOp",EDGE,"E450"),sQuery(id+"F0.wireOp",EDGE,"E451"),sQuery(id+"F0.wireOp",EDGE,"E452"),sQuery(id+"F0.wireOp",EDGE,"E453"),sQuery(id+"F0.wireOp",EDGE,"E454"),sQuery(id+"F0.wireOp",EDGE,"E455"),sQuery(id+"F0.wireOp",EDGE,"E456"),sQuery(id+"F0.wireOp",EDGE,"E457"),sQuery(id+"F0.wireOp",EDGE,"E458"),sQuery(id+"F0.wireOp",EDGE,"E459"),sQuery(id+"F0.wireOp",EDGE,"E460"),sQuery(id+"F0.wireOp",EDGE,"E461"),sQuery(id+"F0.wireOp",EDGE,"E462"),sQuery(id+"F0.wireOp",EDGE,"E463"),sQuery(id+"F0.wireOp",EDGE,"E464"),sQuery(id+"F0.wireOp",EDGE,"E465"),sQuery(id+"F0.wireOp",EDGE,"E466"),sQuery(id+"F0.wireOp",EDGE,"E467"),sQuery(id+"F0.wireOp",EDGE,"E468"),sQuery(id+"F0.wireOp",EDGE,"E469"),sQuery(id+"F0.wireOp",EDGE,"E470"),sQuery(id+"F0.wireOp",EDGE,"E471"),sQuery(id+"F0.wireOp",EDGE,"E472"),sQuery(id+"F0.wireOp",EDGE,"E473"),sQuery(id+"F0.wireOp",EDGE,"E474"),sQuery(id+"F0.wireOp",EDGE,"E475"),sQuery(id+"F0.wireOp",EDGE,"E476"),sQuery(id+"F0.wireOp",EDGE,"E477"),sQuery(id+"F0.wireOp",EDGE,"E478"),sQuery(id+"F0.wireOp",EDGE,"E479"),sQuery(id+"F0.wireOp",EDGE,"E480"),sQuery(id+"F0.wireOp",EDGE,"E481"),sQuery(id+"F0.wireOp",EDGE,"E482"),sQuery(id+"F0.wireOp",EDGE,"E483"),sQuery(id+"F0.wireOp",EDGE,"E484"),sQuery(id+"F0.wireOp",EDGE,"E485"),sQuery(id+"F0.wireOp",EDGE,"E486"),sQuery(id+"F0.wireOp",EDGE,"E487"),sQuery(id+"F0.wireOp",EDGE,"E488"),sQuery(id+"F0.wireOp",EDGE,"E489"),sQuery(id+"F0.wireOp",EDGE,"E490"),sQuery(id+"F0.wireOp",EDGE,"E491"),sQuery(id+"F0.wireOp",EDGE,"E492"),sQuery(id+"F0.wireOp",EDGE,"E493"),sQuery(id+"F0.wireOp",EDGE,"E494"),sQuery(id+"F0.wireOp",EDGE,"E495"),sQuery(id+"F0.wireOp",EDGE,"E496"),sQuery(id+"F0.wireOp",EDGE,"E497"),sQuery(id+"F0.wireOp",EDGE,"E498"),sQuery(id+"F0.wireOp",EDGE,"E499"),sQuery(id+"F0.wireOp",EDGE,"E500"),sQuery(id+"F0.wireOp",EDGE,"E501"),sQuery(id+"F0.wireOp",EDGE,"E502"),sQuery(id+"F0.wireOp",EDGE,"E503"),sQuery(id+"F0.wireOp",EDGE,"E504"),sQuery(id+"F0.wireOp",EDGE,"E505"),sQuery(id+"F0.wireOp",EDGE,"E506"),sQuery(id+"F0.wireOp",EDGE,"E507"),sQuery(id+"F0.wireOp",EDGE,"E508"),sQuery(id+"F0.wireOp",EDGE,"E509"),sQuery(id+"F0.wireOp",EDGE,"E510"),sQuery(id+"F0.wireOp",EDGE,"E511"),sQuery(id+"F0.wireOp",EDGE,"E512"),sQuery(id+"F0.wireOp",EDGE,"E513"),sQuery(id+"F0.wireOp",EDGE,"E514"),sQuery(id+"F0.wireOp",EDGE,"E515"),sQuery(id+"F0.wireOp",EDGE,"E516"),sQuery(id+"F0.wireOp",EDGE,"E517"),sQuery(id+"F0.wireOp",EDGE,"E518"),sQuery(id+"F0.wireOp",EDGE,"E519"),sQuery(id+"F0.wireOp",EDGE,"E520"),sQuery(id+"F0.wireOp",EDGE,"E521"),sQuery(id+"F0.wireOp",EDGE,"E522"),sQuery(id+"F0.wireOp",EDGE,"E523"),sQuery(id+"F0.wireOp",EDGE,"E524"),sQuery(id+"F0.wireOp",EDGE,"E525"),sQuery(id+"F0.wireOp",EDGE,"E526"),sQuery(id+"F0.wireOp",EDGE,"E527"),sQuery(id+"F0.wireOp",EDGE,"E528"),sQuery(id+"F0.wireOp",EDGE,"E529"),sQuery(id+"F0.wireOp",EDGE,"E530"),sQuery(id+"F0.wireOp",EDGE,"E531"),sQuery(id+"F0.wireOp",EDGE,"E532"),sQuery(id+"F0.wireOp",EDGE,"E533"),sQuery(id+"F0.wireOp",EDGE,"E534"),sQuery(id+"F0.wireOp",EDGE,"E535"),sQuery(id+"F0.wireOp",EDGE,"E536"),sQuery(id+"F0.wireOp",EDGE,"E537"),sQuery(id+"F0.wireOp",EDGE,"E538"),sQuery(id+"F0.wireOp",EDGE,"E539"),sQuery(id+"F0.wireOp",EDGE,"E540"),sQuery(id+"F0.wireOp",EDGE,"E541"),sQuery(id+"F0.wireOp",EDGE,"E542"),sQuery(id+"F0.wireOp",EDGE,"E543"),sQuery(id+"F0.wireOp",EDGE,"E544"),sQuery(id+"F0.wireOp",EDGE,"E545"),sQuery(id+"F0.wireOp",EDGE,"E546"),sQuery(id+"F0.wireOp",EDGE,"E547"),sQuery(id+"F0.wireOp",EDGE,"E548"),sQuery(id+"F0.wireOp",EDGE,"E549"),sQuery(id+"F0.wireOp",EDGE,"E550"),sQuery(id+"F0.wireOp",EDGE,"E551"),sQuery(id+"F0.wireOp",EDGE,"E552"),sQuery(id+"F0.wireOp",EDGE,"E553"),sQuery(id+"F0.wireOp",EDGE,"E554"),sQuery(id+"F0.wireOp",EDGE,"E555"),sQuery(id+"F0.wireOp",EDGE,"E556"),sQuery(id+"F0.wireOp",EDGE,"E557"),sQuery(id+"F0.wireOp",EDGE,"E558"),sQuery(id+"F0.wireOp",EDGE,"E559"),sQuery(id+"F0.wireOp",EDGE,"E560"),sQuery(id+"F0.wireOp",EDGE,"E561"),sQuery(id+"F0.wireOp",EDGE,"E562"),sQuery(id+"F0.wireOp",EDGE,"E563"),sQuery(id+"F0.wireOp",EDGE,"E564"),sQuery(id+"F0.wireOp",EDGE,"E565"),sQuery(id+"F0.wireOp",EDGE,"E566"),sQuery(id+"F0.wireOp",EDGE,"E567"),sQuery(id+"F0.wireOp",EDGE,"E568"),sQuery(id+"F0.wireOp",EDGE,"E569"),sQuery(id+"F0.wireOp",EDGE,"E570"),sQuery(id+"F0.wireOp",EDGE,"E571"),sQuery(id+"F0.wireOp",EDGE,"E572"),sQuery(id+"F0.wireOp",EDGE,"E573"),sQuery(id+"F0.wireOp",EDGE,"E574"),sQuery(id+"F0.wireOp",EDGE,"E575"),sQuery(id+"F0.wireOp",EDGE,"E576"),sQuery(id+"F0.wireOp",EDGE,"E577"),sQuery(id+"F0.wireOp",EDGE,"E578"),sQuery(id+"F0.wireOp",EDGE,"E579"),sQuery(id+"F0.wireOp",EDGE,"E580"),sQuery(id+"F0.wireOp",EDGE,"E581"),sQuery(id+"F0.wireOp",EDGE,"E582"),sQuery(id+"F0.wireOp",EDGE,"E583"),sQuery(id+"F0.wireOp",EDGE,"E584"),sQuery(id+"F0.wireOp",EDGE,"E585"),sQuery(id+"F0.wireOp",EDGE,"E586"),sQuery(id+"F0.wireOp",EDGE,"E587"),sQuery(id+"F0.wireOp",EDGE,"E588"),sQuery(id+"F0.wireOp",EDGE,"E589"),sQuery(id+"F0.wireOp",EDGE,"E590"),sQuery(id+"F0.wireOp",EDGE,"E591"),sQuery(id+"F0.wireOp",EDGE,"E592"),sQuery(id+"F0.wireOp",EDGE,"E593"),sQuery(id+"F0.wireOp",EDGE,"E594"),sQuery(id+"F0.wireOp",EDGE,"E595"),sQuery(id+"F0.wireOp",EDGE,"E596"),sQuery(id+"F0.wireOp",EDGE,"E597"),sQuery(id+"F0.wireOp",EDGE,"E598"),sQuery(id+"F0.wireOp",EDGE,"E599"),sQuery(id+"F0.wireOp",EDGE,"E600"),sQuery(id+"F0.wireOp",EDGE,"E601"),sQuery(id+"F0.wireOp",EDGE,"E602"),sQuery(id+"F0.wireOp",EDGE,"E603"),sQuery(id+"F0.wireOp",EDGE,"E604"),sQuery(id+"F0.wireOp",EDGE,"E605"),sQuery(id+"F0.wireOp",EDGE,"E606"),sQuery(id+"F0.wireOp",EDGE,"E607"),sQuery(id+"F0.wireOp",EDGE,"E608"),sQuery(id+"F0.wireOp",EDGE,"E609"),sQuery(id+"F0.wireOp",EDGE,"E610"),sQuery(id+"F0.wireOp",EDGE,"E611"),sQuery(id+"F0.wireOp",EDGE,"E612"),sQuery(id+"F0.wireOp",EDGE,"E613"),sQuery(id+"F0.wireOp",EDGE,"E614"),sQuery(id+"F0.wireOp",EDGE,"E615"),sQuery(id+"F0.wireOp",EDGE,"E616"),sQuery(id+"F0.wireOp",EDGE,"E617"),sQuery(id+"F0.wireOp",EDGE,"E618"),sQuery(id+"F0.wireOp",EDGE,"E619"),sQuery(id+"F0.wireOp",EDGE,"E620"),sQuery(id+"F0.wireOp",EDGE,"E621"),sQuery(id+"F0.wireOp",EDGE,"E622"),sQuery(id+"F0.wireOp",EDGE,"E623"),sQuery(id+"F0.wireOp",EDGE,"E624"),sQuery(id+"F0.wireOp",EDGE,"E625")])]});
            var Q1;
            Q1=makeQuery(id+"F1.opExtrude","CAP_VERTEX",VERTEX,{"disambiguationData":[OSD([sQuery(id+"F0.wireOp",EDGE,"E76"),sQuery(id+"F0.wireOp",EDGE,"E77")])],"isStart":false});
            transform(context, id + "F2", {"entities" : qUnion([Q0]), "transformType" : TransformType.SCALE_UNIFORMLY, "scale" : 19, "scalePoint" : qUnion([Q1]), "makeCopy" : false});
        }
        {
            var Q0;
            Q0=qCreatedBy(makeId("Front.planeOp"),FACE);
            cPlane(context, id + "F3", {"entities" : qUnion([Q0]), "cplaneType" : CPlaneType.OFFSET, "offset" : 25 * mm, "width" : 150 * mm, "height" : 150 * mm});
        }
        {
            var Q0;
            Q0=qCreatedBy(id+"F3.planeOp",FACE);
            var sketch = newSketch(context, id + "F4", { "sketchPlane" : qUnion([Q0])});
            skCircle(sketch, "E626", {"center": v(2.84, 74.37) * mm, "radius": 9.05 * mm});
            skArc(sketch, "E627", {"start": v(7.5, 87.9) * mm, "mid": v(2.46, 91.76) * mm, "end": v(-2.58, 87.9) * mm});
            skLineSegment(sketch, "E628", {"start": v(-2.58, 87.9) * mm, "end": v(-2.58, 81.62) * mm});
            skLineSegment(sketch, "E629", {"start": v(7.5, 87.9) * mm, "end": v(7.5, 82.13) * mm});
            skSolve(sketch);
        }
        {
            var Q0;
            Q0 = qSketchRegion(id + "F4", true);
            extrude(context, id + "F5", {"entities" : qUnion([Q0]), "operationType" : NewBodyOperationType.REMOVE, "oppositeDirection" : true, "depth" : 30 * mm, "offsetDistance" : 25 * mm});
        }
    });
